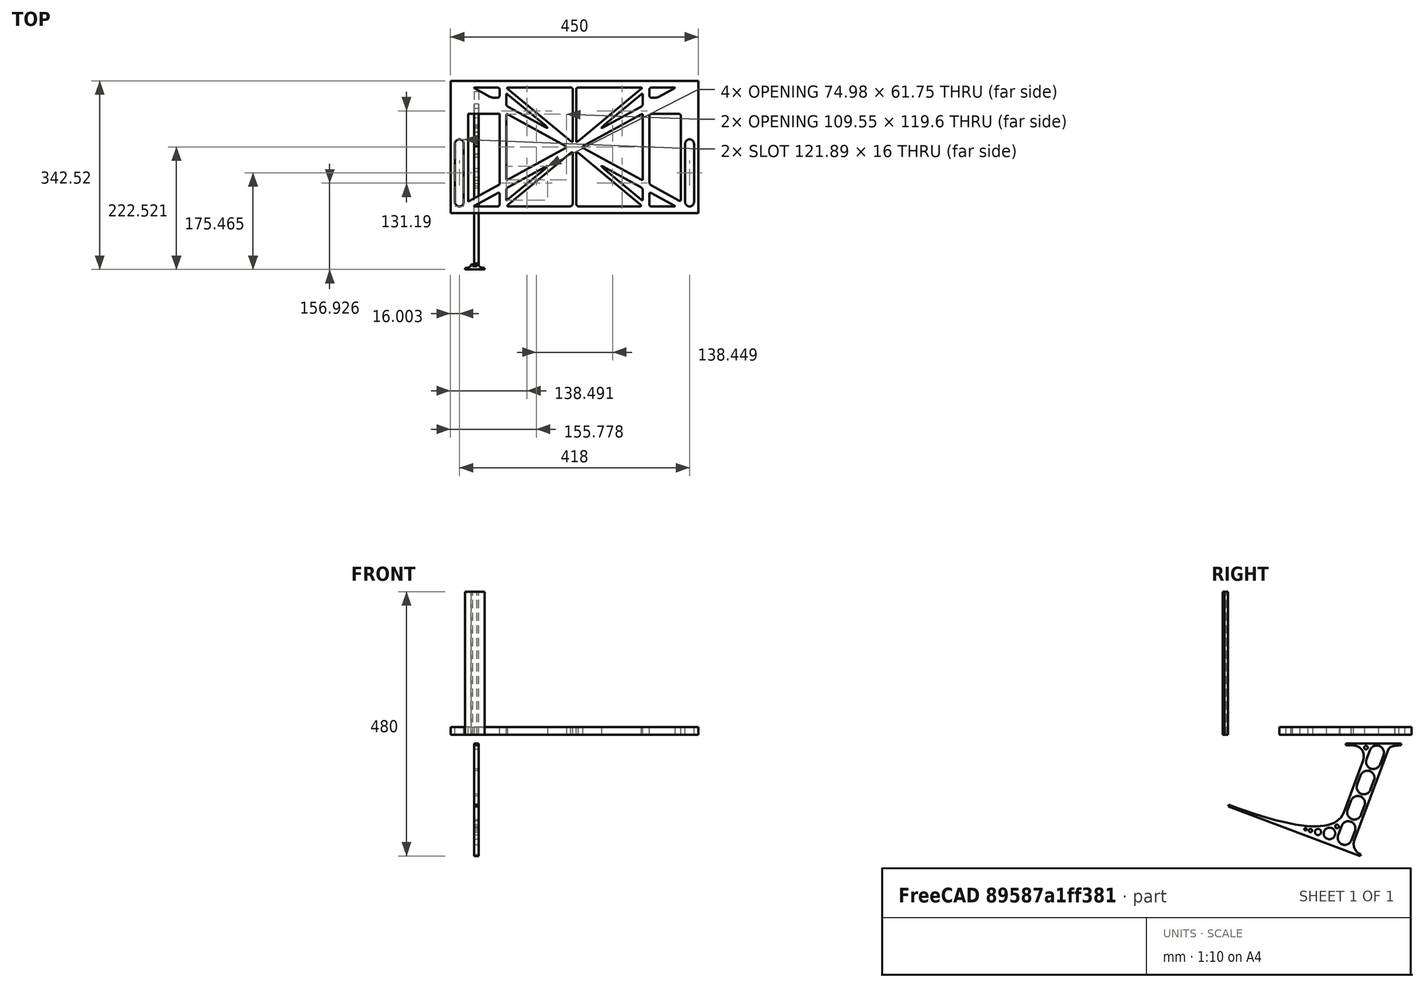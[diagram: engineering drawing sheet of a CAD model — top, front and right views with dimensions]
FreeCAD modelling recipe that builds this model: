
FCSTD DOCUMENT  (FreeCAD 0.19R0.19.2)
Label: laptopStand142FCStd
License: All rights reserved
LicenseURL: http://en.wikipedia.org/wiki/All_rights_reserved
objects: Sketcher::SketchObject×4, Part::Extrusion×3
note: 7 computed .brp shape members not serialized (recipe doc carries the construction recipe); baked Part::Feature solids carry a one-line shape summary decoded from their .brp

FEATURE [Sketcher::SketchObject] Sketch
  FullyConstrained = false
  sketch-geometry (349):
    g0: LineSegment StartX=-10.9272 StartY=-82.7794 StartZ=0 EndX=46.0728 EndY=-51.4823 EndZ=0
    g1: LineSegment StartX=-10.9272 StartY=76.4095 StartZ=0 EndX=-10.9272 EndY=-82.7794 EndZ=0
    g2: LineSegment StartX=46.0728 StartY=76.4095 StartZ=0 EndX=46.0728 EndY=-51.4823 EndZ=0
    g3: LineSegment StartX=-42.9272 StartY=136.221 StartZ=0 EndX=-42.9272 EndY=-103.779 EndZ=0
    g4: LineSegment StartX=407.073 StartY=136.221 StartZ=0 EndX=407.073 EndY=-103.779 EndZ=0
    g5: ArcOfCircle CenterX=-26.9272 CenterY=-83.7794 CenterZ=0 NormalX=0 NormalY=0 NormalZ=1 AngleXU=0 Radius=8 StartAngle=3.14159 EndAngle=6.28319
    g6: ArcOfCircle CenterX=391.073 CenterY=22.1087 CenterZ=0 NormalX=0 NormalY=0 NormalZ=1 AngleXU=0 Radius=8 StartAngle=-4.4e-15 EndAngle=3.14159
    g7: LineSegment StartX=399.073 StartY=22.1087 StartZ=0 EndX=399.073 EndY=-83.7794 EndZ=0
    g8: LineSegment StartX=383.073 StartY=22.1087 StartZ=0 EndX=383.073 EndY=-83.7794 EndZ=0
    g9: ArcOfCircle CenterX=391.073 CenterY=-83.7794 CenterZ=0 NormalX=0 NormalY=0 NormalZ=1 AngleXU=0 Radius=8 StartAngle=3.14159 EndAngle=6.28319
    g10: Circle CenterX=175.022 CenterY=27.0628 CenterZ=0 NormalX=0 NormalY=0 NormalZ=1 AngleXU=0 Radius=1
    g11: Circle CenterX=179.022 CenterY=24.8665 CenterZ=0 NormalX=0 NormalY=0 NormalZ=1 AngleXU=0 Radius=1
    g12: Circle CenterX=179.022 CenterY=27.0628 CenterZ=0 NormalX=0 NormalY=0 NormalZ=1 AngleXU=0 Radius=1
    g13: BSplineCurve PolesCount=3 KnotsCount=2 Degree=2 IsPeriodic=0
    g14: GeomPoint X=175.022 Y=27.0628 Z=0
    g15: GeomPoint X=179.022 Y=27.0628 Z=0
    g16: Circle CenterX=189.124 CenterY=27.0628 CenterZ=0 NormalX=0 NormalY=0 NormalZ=1 AngleXU=0 Radius=1
    g17: Circle CenterX=185.124 CenterY=24.8665 CenterZ=0 NormalX=0 NormalY=0 NormalZ=1 AngleXU=0 Radius=1
    g18: Circle CenterX=185.124 CenterY=27.0628 CenterZ=0 NormalX=0 NormalY=0 NormalZ=1 AngleXU=0 Radius=1
    g19: BSplineCurve PolesCount=3 KnotsCount=2 Degree=2 IsPeriodic=0
    g20: GeomPoint X=189.124 Y=27.0628 Z=0
    g21: GeomPoint X=185.124 Y=27.0628 Z=0
    g22: Circle CenterX=175.022 CenterY=5.37834 CenterZ=0 NormalX=0 NormalY=0 NormalZ=1 AngleXU=0 Radius=1
    g23: Circle CenterX=179.022 CenterY=7.57463 CenterZ=0 NormalX=0 NormalY=0 NormalZ=1 AngleXU=0 Radius=1
    g24: Circle CenterX=179.022 CenterY=5.34704 CenterZ=0 NormalX=0 NormalY=0 NormalZ=1 AngleXU=0 Radius=1
    g25: BSplineCurve PolesCount=3 KnotsCount=2 Degree=2 IsPeriodic=0
    g26: GeomPoint X=175.022 Y=5.37834 Z=0
    g27: GeomPoint X=179.022 Y=5.34704 Z=0
    g28: Circle CenterX=189.124 CenterY=5.37834 CenterZ=0 NormalX=0 NormalY=0 NormalZ=1 AngleXU=0 Radius=1
    g29: Circle CenterX=185.124 CenterY=7.57463 CenterZ=0 NormalX=0 NormalY=0 NormalZ=1 AngleXU=0 Radius=1
    g30: Circle CenterX=185.124 CenterY=5.34704 CenterZ=0 NormalX=0 NormalY=0 NormalZ=1 AngleXU=0 Radius=1
    g31: BSplineCurve PolesCount=3 KnotsCount=2 Degree=2 IsPeriodic=0
    g32: GeomPoint X=189.124 Y=5.37834 Z=0
    g33: GeomPoint X=185.124 Y=5.34704 Z=0
    g34: Circle CenterX=165.871 CenterY=18.1458 CenterZ=0 NormalX=0 NormalY=0 NormalZ=1 AngleXU=0 Radius=1
    g35: Circle CenterX=169.377 CenterY=16.2206 CenterZ=0 NormalX=0 NormalY=0 NormalZ=1 AngleXU=0 Radius=1
    g36: Circle CenterX=165.871 CenterY=14.2954 CenterZ=0 NormalX=0 NormalY=0 NormalZ=1 AngleXU=0 Radius=1
    g37: BSplineCurve PolesCount=3 KnotsCount=2 Degree=2 IsPeriodic=0
    g38: GeomPoint X=165.871 Y=18.1458 Z=0
    g39: GeomPoint X=165.871 Y=14.2954 Z=0
    g40: Circle CenterX=198.275 CenterY=18.1458 CenterZ=0 NormalX=0 NormalY=0 NormalZ=1 AngleXU=0 Radius=1
    g41: Circle CenterX=194.768 CenterY=16.2206 CenterZ=0 NormalX=0 NormalY=0 NormalZ=1 AngleXU=0 Radius=1
    g42: Circle CenterX=198.275 CenterY=14.2954 CenterZ=0 NormalX=0 NormalY=0 NormalZ=1 AngleXU=0 Radius=1
    g43: BSplineCurve PolesCount=3 KnotsCount=2 Degree=2 IsPeriodic=0
    g44: GeomPoint X=198.275 Y=18.1458 Z=0
    g45: GeomPoint X=198.275 Y=14.2954 Z=0
    g46: LineSegment StartX=407.073 StartY=-103.779 StartZ=0 EndX=-42.9272 EndY=-103.779 EndZ=0
    g47: LineSegment StartX=407.073 StartY=136.221 StartZ=0 EndX=-42.9272 EndY=136.221 EndZ=0
    g48: LineSegment StartX=46.0728 StartY=76.4095 StartZ=0 EndX=-10.9272 EndY=76.4095 EndZ=0
    g49: Circle CenterX=125.607 CenterY=54.1951 CenterZ=0 NormalX=0 NormalY=0 NormalZ=1 AngleXU=0 Radius=1
    g50: Circle CenterX=139.632 CenterY=46.4944 CenterZ=0 NormalX=0 NormalY=0 NormalZ=1 AngleXU=0 Radius=1
    g51: Circle CenterX=127.326 CenterY=56.7187 CenterZ=0 NormalX=0 NormalY=0 NormalZ=1 AngleXU=0 Radius=1
    g52: BSplineCurve PolesCount=3 KnotsCount=2 Degree=2 IsPeriodic=0
    g53: GeomPoint X=125.607 Y=54.1951 Z=0
    g54: GeomPoint X=127.326 Y=56.7187 Z=0
    g55: Circle CenterX=236.821 CenterY=56.7187 CenterZ=0 NormalX=0 NormalY=0 NormalZ=1 AngleXU=0 Radius=1
    g56: Circle CenterX=224.513 CenterY=46.4944 CenterZ=0 NormalX=0 NormalY=0 NormalZ=1 AngleXU=0 Radius=1
    g57: Circle CenterX=238.538 CenterY=54.1951 CenterZ=0 NormalX=0 NormalY=0 NormalZ=1 AngleXU=0 Radius=1
    g58: BSplineCurve PolesCount=3 KnotsCount=2 Degree=2 IsPeriodic=0
    g59: GeomPoint X=236.821 Y=56.7187 Z=0
    g60: GeomPoint X=238.538 Y=54.1951 Z=0
    g61: Circle CenterX=238.538 CenterY=-21.7539 CenterZ=0 NormalX=0 NormalY=0 NormalZ=1 AngleXU=0 Radius=1
    g62: Circle CenterX=224.513 CenterY=-14.0532 CenterZ=0 NormalX=0 NormalY=0 NormalZ=1 AngleXU=0 Radius=1
    g63: Circle CenterX=236.821 CenterY=-24.2775 CenterZ=0 NormalX=0 NormalY=0 NormalZ=1 AngleXU=0 Radius=1
    g64: BSplineCurve PolesCount=3 KnotsCount=2 Degree=2 IsPeriodic=0
    g65: GeomPoint X=238.538 Y=-21.7539 Z=0
    g66: GeomPoint X=236.821 Y=-24.2775 Z=0
    g67: Circle CenterX=125.607 CenterY=-21.7539 CenterZ=0 NormalX=0 NormalY=0 NormalZ=1 AngleXU=0 Radius=1
    g68: Circle CenterX=139.632 CenterY=-14.0532 CenterZ=0 NormalX=0 NormalY=0 NormalZ=1 AngleXU=0 Radius=1
    g69: Circle CenterX=127.325 CenterY=-24.2775 CenterZ=0 NormalX=0 NormalY=0 NormalZ=1 AngleXU=0 Radius=1
    g70: BSplineCurve PolesCount=3 KnotsCount=2 Degree=2 IsPeriodic=0
    g71: GeomPoint X=125.607 Y=-21.7539 Z=0
    g72: GeomPoint X=127.325 Y=-24.2775 Z=0
    g73: Circle CenterX=302.996 CenterY=111.695 CenterZ=0 NormalX=0 NormalY=0 NormalZ=1 AngleXU=0 Radius=1
    g74: Circle CenterX=306.073 CenterY=114.251 CenterZ=0 NormalX=0 NormalY=0 NormalZ=1 AngleXU=0 Radius=1
    g75: Circle CenterX=306.073 CenterY=110.251 CenterZ=0 NormalX=0 NormalY=0 NormalZ=1 AngleXU=0 Radius=1
    g76: BSplineCurve PolesCount=3 KnotsCount=2 Degree=2 IsPeriodic=0
    g77: GeomPoint X=302.996 Y=111.695 Z=0
    g78: GeomPoint X=306.073 Y=110.251 Z=0
    g79: Circle CenterX=306.073 CenterY=95.2763 CenterZ=0 NormalX=0 NormalY=0 NormalZ=1 AngleXU=0 Radius=1
    g80: Circle CenterX=306.073 CenterY=91.2763 CenterZ=0 NormalX=0 NormalY=0 NormalZ=1 AngleXU=0 Radius=1
    g81: Circle CenterX=302.567 CenterY=89.3511 CenterZ=0 NormalX=0 NormalY=0 NormalZ=1 AngleXU=0 Radius=1
    g82: BSplineCurve PolesCount=3 KnotsCount=2 Degree=2 IsPeriodic=0
    g83: GeomPoint X=306.073 Y=95.2763 Z=0
    g84: GeomPoint X=302.567 Y=89.3511 Z=0
    g85: LineSegment StartX=306.073 StartY=110.251 StartZ=0 EndX=306.073 EndY=95.2763 EndZ=0
    g86: LineSegment StartX=302.996 StartY=111.695 StartZ=0 EndX=236.821 EndY=56.7187 EndZ=0
    g87: LineSegment StartX=238.538 StartY=54.1951 StartZ=0 EndX=302.567 EndY=89.3511 EndZ=0
    g88: Circle CenterX=61.1496 CenterY=111.695 CenterZ=0 NormalX=0 NormalY=0 NormalZ=1 AngleXU=0 Radius=1
    g89: Circle CenterX=58.0728 CenterY=114.251 CenterZ=0 NormalX=0 NormalY=0 NormalZ=1 AngleXU=0 Radius=1
    g90: Circle CenterX=58.0728 CenterY=110.251 CenterZ=0 NormalX=0 NormalY=0 NormalZ=1 AngleXU=0 Radius=1
    g91: BSplineCurve PolesCount=3 KnotsCount=2 Degree=2 IsPeriodic=0
    g92: GeomPoint X=61.1496 Y=111.695 Z=0
    g93: GeomPoint X=58.0728 Y=110.251 Z=0
    g94: Circle CenterX=61.5791 CenterY=89.3511 CenterZ=0 NormalX=0 NormalY=0 NormalZ=1 AngleXU=0 Radius=1
    g95: Circle CenterX=58.0728 CenterY=91.2763 CenterZ=0 NormalX=0 NormalY=0 NormalZ=1 AngleXU=0 Radius=1
    g96: Circle CenterX=58.0728 CenterY=95.2763 CenterZ=0 NormalX=0 NormalY=0 NormalZ=1 AngleXU=0 Radius=1
    g97: BSplineCurve PolesCount=3 KnotsCount=2 Degree=2 IsPeriodic=0
    g98: GeomPoint X=61.5791 Y=89.3511 Z=0
    g99: GeomPoint X=58.0728 Y=95.2763 Z=0
    g100: LineSegment StartX=58.0728 StartY=110.251 StartZ=0 EndX=58.0728 EndY=95.2763 EndZ=0
    g101: LineSegment StartX=61.1496 StartY=111.695 StartZ=0 EndX=127.326 EndY=56.7187 EndZ=0
    g102: LineSegment StartX=125.607 StartY=54.1951 StartZ=0 EndX=61.5791 EndY=89.3511 EndZ=0
    g103: Circle CenterX=61.5791 CenterY=-56.9099 CenterZ=0 NormalX=0 NormalY=0 NormalZ=1 AngleXU=0 Radius=1
    g104: Circle CenterX=58.0728 CenterY=-58.8351 CenterZ=0 NormalX=0 NormalY=0 NormalZ=1 AngleXU=0 Radius=1
    g105: Circle CenterX=58.0728 CenterY=-62.8351 CenterZ=0 NormalX=0 NormalY=0 NormalZ=1 AngleXU=0 Radius=1
    g106: BSplineCurve PolesCount=3 KnotsCount=2 Degree=2 IsPeriodic=0
    g107: GeomPoint X=61.5791 Y=-56.9099 Z=0
    g108: GeomPoint X=58.0728 Y=-62.8351 Z=0
    g109: Circle CenterX=58.0728 CenterY=-77.8102 CenterZ=0 NormalX=0 NormalY=0 NormalZ=1 AngleXU=0 Radius=1
    g110: Circle CenterX=58.0728 CenterY=-81.8102 CenterZ=0 NormalX=0 NormalY=0 NormalZ=1 AngleXU=0 Radius=1
    g111: Circle CenterX=61.1496 CenterY=-79.2541 CenterZ=0 NormalX=0 NormalY=0 NormalZ=1 AngleXU=0 Radius=1
    g112: BSplineCurve PolesCount=3 KnotsCount=2 Degree=2 IsPeriodic=0
    g113: GeomPoint X=58.0728 Y=-77.8102 Z=0
    g114: GeomPoint X=61.1496 Y=-79.2541 Z=0
    g115: LineSegment StartX=58.0728 StartY=-62.8351 StartZ=0 EndX=58.0728 EndY=-77.8102 EndZ=0
    g116: LineSegment StartX=61.1496 StartY=-79.2541 StartZ=0 EndX=127.325 EndY=-24.2775 EndZ=0
    g117: LineSegment StartX=125.607 StartY=-21.7539 StartZ=0 EndX=61.5791 EndY=-56.9099 EndZ=0
    g118: Circle CenterX=302.567 CenterY=-56.9099 CenterZ=0 NormalX=0 NormalY=0 NormalZ=1 AngleXU=0 Radius=1
    g119: Circle CenterX=306.073 CenterY=-58.8351 CenterZ=0 NormalX=0 NormalY=0 NormalZ=1 AngleXU=0 Radius=1
    g120: Circle CenterX=306.073 CenterY=-62.8351 CenterZ=0 NormalX=0 NormalY=0 NormalZ=1 AngleXU=0 Radius=1
    g121: BSplineCurve PolesCount=3 KnotsCount=2 Degree=2 IsPeriodic=0
    g122: GeomPoint X=302.567 Y=-56.9099 Z=0
    g123: GeomPoint X=306.073 Y=-62.8351 Z=0
    g124: Circle CenterX=302.996 CenterY=-79.2541 CenterZ=0 NormalX=0 NormalY=0 NormalZ=1 AngleXU=0 Radius=1
    g125: Circle CenterX=306.073 CenterY=-81.8102 CenterZ=0 NormalX=0 NormalY=0 NormalZ=1 AngleXU=0 Radius=1
    g126: Circle CenterX=306.073 CenterY=-77.8102 CenterZ=0 NormalX=0 NormalY=0 NormalZ=1 AngleXU=0 Radius=1
    g127: BSplineCurve PolesCount=3 KnotsCount=2 Degree=2 IsPeriodic=0
    g128: GeomPoint X=302.996 Y=-79.2541 Z=0
    g129: GeomPoint X=306.073 Y=-77.8102 Z=0
    g130: LineSegment StartX=306.073 StartY=-62.8351 StartZ=0 EndX=306.073 EndY=-77.8102 EndZ=0
    g131: LineSegment StartX=302.996 StartY=-79.2541 StartZ=0 EndX=236.821 EndY=-24.2775 EndZ=0
    g132: LineSegment StartX=238.538 StartY=-21.7539 StartZ=0 EndX=302.567 EndY=-56.9099 EndZ=0
    g133: Circle CenterX=61.6457 CenterY=-88.8112 CenterZ=0 NormalX=0 NormalY=0 NormalZ=1 AngleXU=0 Radius=1
    g134: Circle CenterX=58.0728 CenterY=-91.7794 CenterZ=0 NormalX=0 NormalY=0 NormalZ=1 AngleXU=0 Radius=1
    g135: Circle CenterX=63.9135 CenterY=-91.7794 CenterZ=0 NormalX=0 NormalY=0 NormalZ=1 AngleXU=0 Radius=1
    g136: BSplineCurve PolesCount=3 KnotsCount=2 Degree=2 IsPeriodic=0
    g137: GeomPoint X=61.6457 Y=-88.8112 Z=0
    g138: GeomPoint X=63.9135 Y=-91.7794 Z=0
    g139: Circle CenterX=179.022 CenterY=-85.8163 CenterZ=0 NormalX=0 NormalY=0 NormalZ=1 AngleXU=0 Radius=1
    g140: Circle CenterX=179.022 CenterY=-91.7794 CenterZ=0 NormalX=0 NormalY=0 NormalZ=1 AngleXU=0 Radius=1
    g141: Circle CenterX=171.895 CenterY=-91.7794 CenterZ=0 NormalX=0 NormalY=0 NormalZ=1 AngleXU=0 Radius=1
    g142: BSplineCurve PolesCount=3 KnotsCount=2 Degree=2 IsPeriodic=0
    g143: GeomPoint X=179.022 Y=-85.8163 Z=0
    g144: GeomPoint X=171.895 Y=-91.7794 Z=0
    g145: Circle CenterX=185.124 CenterY=-86.2028 CenterZ=0 NormalX=0 NormalY=0 NormalZ=1 AngleXU=0 Radius=1
    g146: Circle CenterX=185.124 CenterY=-91.7794 CenterZ=0 NormalX=0 NormalY=0 NormalZ=1 AngleXU=0 Radius=1
    g147: Circle CenterX=191.747 CenterY=-91.7794 CenterZ=0 NormalX=0 NormalY=0 NormalZ=1 AngleXU=0 Radius=1
    g148: BSplineCurve PolesCount=3 KnotsCount=2 Degree=2 IsPeriodic=0
    g149: GeomPoint X=185.124 Y=-86.2028 Z=0
    g150: GeomPoint X=191.747 Y=-91.7794 Z=0
    g151: Circle CenterX=299.888 CenterY=-86.6413 CenterZ=0 NormalX=0 NormalY=0 NormalZ=1 AngleXU=0 Radius=1
    g152: Circle CenterX=306.073 CenterY=-91.7794 CenterZ=0 NormalX=0 NormalY=0 NormalZ=1 AngleXU=0 Radius=1
    g153: Circle CenterX=298.776 CenterY=-91.7794 CenterZ=0 NormalX=0 NormalY=0 NormalZ=1 AngleXU=0 Radius=1
    g154: BSplineCurve PolesCount=3 KnotsCount=2 Degree=2 IsPeriodic=0
    g155: GeomPoint X=299.888 Y=-86.6413 Z=0
    g156: GeomPoint X=298.776 Y=-91.7794 Z=0
    g157: LineSegment StartX=189.124 StartY=5.37834 StartZ=0 EndX=299.888 EndY=-86.6413 EndZ=0
    g158: LineSegment StartX=298.776 StartY=-91.7794 StartZ=0 EndX=191.747 EndY=-91.7794 EndZ=0
    g159: LineSegment StartX=185.124 StartY=-86.2028 StartZ=0 EndX=185.124 EndY=5.34704 EndZ=0
    g160: LineSegment StartX=179.022 StartY=5.34704 StartZ=0 EndX=179.022 EndY=-85.8163 EndZ=0
    g161: LineSegment StartX=171.895 StartY=-91.7794 StartZ=0 EndX=63.9135 EndY=-91.7794 EndZ=0
    g162: LineSegment StartX=61.6457 StartY=-88.8112 StartZ=0 EndX=175.022 EndY=5.37834 EndZ=0
    g163: Circle CenterX=302.073 CenterY=124.221 CenterZ=0 NormalX=0 NormalY=0 NormalZ=1 AngleXU=0 Radius=1
    g164: Circle CenterX=306.073 CenterY=124.221 CenterZ=0 NormalX=0 NormalY=0 NormalZ=1 AngleXU=0 Radius=1
    g165: Circle CenterX=302.996 CenterY=121.665 CenterZ=0 NormalX=0 NormalY=0 NormalZ=1 AngleXU=0 Radius=1
    g166: BSplineCurve PolesCount=3 KnotsCount=2 Degree=2 IsPeriodic=0
    g167: GeomPoint X=302.073 Y=124.221 Z=0
    g168: GeomPoint X=302.996 Y=121.665 Z=0
    g169: Circle CenterX=189.124 CenterY=124.221 CenterZ=0 NormalX=0 NormalY=0 NormalZ=1 AngleXU=0 Radius=1
    g170: Circle CenterX=185.124 CenterY=124.221 CenterZ=0 NormalX=0 NormalY=0 NormalZ=1 AngleXU=0 Radius=1
    g171: Circle CenterX=185.124 CenterY=120.221 CenterZ=0 NormalX=0 NormalY=0 NormalZ=1 AngleXU=0 Radius=1
    g172: BSplineCurve PolesCount=3 KnotsCount=2 Degree=2 IsPeriodic=0
    g173: GeomPoint X=189.124 Y=124.221 Z=0
    g174: GeomPoint X=185.124 Y=120.221 Z=0
    g175: Circle CenterX=175.022 CenterY=124.221 CenterZ=0 NormalX=0 NormalY=0 NormalZ=1 AngleXU=0 Radius=1
    g176: Circle CenterX=179.022 CenterY=124.221 CenterZ=0 NormalX=0 NormalY=0 NormalZ=1 AngleXU=0 Radius=1
    g177: Circle CenterX=179.022 CenterY=120.221 CenterZ=0 NormalX=0 NormalY=0 NormalZ=1 AngleXU=0 Radius=1
    g178: BSplineCurve PolesCount=3 KnotsCount=2 Degree=2 IsPeriodic=0
    g179: GeomPoint X=175.022 Y=124.221 Z=0
    g180: GeomPoint X=179.022 Y=120.221 Z=0
    g181: Circle CenterX=62.0728 CenterY=124.221 CenterZ=0 NormalX=0 NormalY=0 NormalZ=1 AngleXU=0 Radius=1
    g182: Circle CenterX=58.0728 CenterY=124.221 CenterZ=0 NormalX=0 NormalY=0 NormalZ=1 AngleXU=0 Radius=1
    g183: Circle CenterX=61.1496 CenterY=121.665 CenterZ=0 NormalX=0 NormalY=0 NormalZ=1 AngleXU=0 Radius=1
    g184: BSplineCurve PolesCount=3 KnotsCount=2 Degree=2 IsPeriodic=0
    g185: GeomPoint X=62.0728 Y=124.221 Z=0
    g186: GeomPoint X=61.1496 Y=121.665 Z=0
    g187: LineSegment StartX=62.0728 StartY=124.221 StartZ=0 EndX=175.022 EndY=124.221 EndZ=0
    g188: LineSegment StartX=179.022 StartY=120.221 StartZ=0 EndX=179.022 EndY=27.0628 EndZ=0
    g189: LineSegment StartX=185.124 StartY=27.0628 StartZ=0 EndX=185.124 EndY=120.221 EndZ=0
    g190: LineSegment StartX=189.124 StartY=124.221 StartZ=0 EndX=302.073 EndY=124.221 EndZ=0
    g191: LineSegment StartX=302.996 StartY=121.665 StartZ=0 EndX=189.124 EndY=27.0628 EndZ=0
    g192: LineSegment StartX=175.022 StartY=27.0628 StartZ=0 EndX=61.1496 EndY=121.665 EndZ=0
    g193: Circle CenterX=61.5791 CenterY=75.4095 CenterZ=0 NormalX=0 NormalY=0 NormalZ=1 AngleXU=0 Radius=1
    g194: Circle CenterX=58.0728 CenterY=77.3346 CenterZ=0 NormalX=0 NormalY=0 NormalZ=1 AngleXU=0 Radius=1
    g195: Circle CenterX=58.0728 CenterY=73.3346 CenterZ=0 NormalX=0 NormalY=0 NormalZ=1 AngleXU=0 Radius=1
    g196: BSplineCurve PolesCount=3 KnotsCount=2 Degree=2 IsPeriodic=0
    g197: GeomPoint X=61.5791 Y=75.4095 Z=0
    g198: GeomPoint X=58.0728 Y=73.3346 Z=0
    g199: Circle CenterX=58.0728 CenterY=-40.8935 CenterZ=0 NormalX=0 NormalY=0 NormalZ=1 AngleXU=0 Radius=1
    g200: Circle CenterX=58.0728 CenterY=-44.8935 CenterZ=0 NormalX=0 NormalY=0 NormalZ=1 AngleXU=0 Radius=1
    g201: Circle CenterX=61.5791 CenterY=-42.9683 CenterZ=0 NormalX=0 NormalY=0 NormalZ=1 AngleXU=0 Radius=1
    g202: BSplineCurve PolesCount=3 KnotsCount=2 Degree=2 IsPeriodic=0
    g203: GeomPoint X=58.0728 Y=-40.8935 Z=0
    g204: GeomPoint X=61.5791 Y=-42.9683 Z=0
    g205: LineSegment StartX=61.5791 StartY=-42.9683 StartZ=0 EndX=165.871 EndY=14.2954 EndZ=0
    g206: LineSegment StartX=165.871 StartY=18.1458 StartZ=0 EndX=61.5791 EndY=75.4095 EndZ=0
    g207: LineSegment StartX=58.0728 StartY=73.3346 StartZ=0 EndX=58.0728 EndY=-40.8935 EndZ=0
    g208: Circle CenterX=302.567 CenterY=-42.9683 CenterZ=0 NormalX=0 NormalY=0 NormalZ=1 AngleXU=0 Radius=1
    g209: Circle CenterX=306.073 CenterY=-44.8935 CenterZ=0 NormalX=0 NormalY=0 NormalZ=1 AngleXU=0 Radius=1
    g210: Circle CenterX=306.073 CenterY=-40.8935 CenterZ=0 NormalX=0 NormalY=0 NormalZ=1 AngleXU=0 Radius=1
    g211: BSplineCurve PolesCount=3 KnotsCount=2 Degree=2 IsPeriodic=0
    g212: GeomPoint X=302.567 Y=-42.9683 Z=0
    g213: GeomPoint X=306.073 Y=-40.8935 Z=0
    g214: Circle CenterX=306.073 CenterY=73.3346 CenterZ=0 NormalX=0 NormalY=0 NormalZ=1 AngleXU=0 Radius=1
    g215: Circle CenterX=306.073 CenterY=77.3346 CenterZ=0 NormalX=0 NormalY=0 NormalZ=1 AngleXU=0 Radius=1
    g216: Circle CenterX=302.567 CenterY=75.4095 CenterZ=0 NormalX=0 NormalY=0 NormalZ=1 AngleXU=0 Radius=1
    g217: BSplineCurve PolesCount=3 KnotsCount=2 Degree=2 IsPeriodic=0
    g218: GeomPoint X=306.073 Y=73.3346 Z=0
    g219: GeomPoint X=302.567 Y=75.4095 Z=0
    g220: LineSegment StartX=302.567 StartY=-42.9683 StartZ=0 EndX=198.275 EndY=14.2954 EndZ=0
    g221: LineSegment StartX=198.275 StartY=18.1458 StartZ=0 EndX=302.567 EndY=75.4095 EndZ=0
    g222: LineSegment StartX=306.073 StartY=73.3346 StartZ=0 EndX=306.073 EndY=-40.8935 EndZ=0
    g223: LineSegment StartX=322.073 StartY=105.865 StartZ=0 EndX=328.643 EndY=105.865 EndZ=0
    g224: LineSegment StartX=318.073 StartY=120.221 StartZ=0 EndX=318.073 EndY=109.865 EndZ=0
    g225: LineSegment StartX=336.157 StartY=107.779 StartZ=0 EndX=362.567 EndY=122.294 EndZ=0
    g226: Circle CenterX=362.073 CenterY=124.221 CenterZ=0 NormalX=0 NormalY=0 NormalZ=1 AngleXU=0 Radius=1
    g227: Circle CenterX=366.073 CenterY=124.221 CenterZ=0 NormalX=0 NormalY=0 NormalZ=1 AngleXU=0 Radius=1
    g228: Circle CenterX=362.567 CenterY=122.294 CenterZ=0 NormalX=0 NormalY=0 NormalZ=1 AngleXU=0 Radius=1
    g229: BSplineCurve PolesCount=3 KnotsCount=2 Degree=2 IsPeriodic=0
    g230: GeomPoint X=362.073 Y=124.221 Z=0
    g231: GeomPoint X=362.567 Y=122.294 Z=0
    g232: Circle CenterX=322.073 CenterY=124.221 CenterZ=0 NormalX=0 NormalY=0 NormalZ=1 AngleXU=0 Radius=1
    g233: Circle CenterX=318.073 CenterY=124.221 CenterZ=0 NormalX=0 NormalY=0 NormalZ=1 AngleXU=0 Radius=1
    g234: Circle CenterX=318.073 CenterY=120.221 CenterZ=0 NormalX=0 NormalY=0 NormalZ=1 AngleXU=0 Radius=1
    g235: BSplineCurve PolesCount=3 KnotsCount=2 Degree=2 IsPeriodic=0
    g236: GeomPoint X=322.073 Y=124.221 Z=0
    g237: GeomPoint X=318.073 Y=120.221 Z=0
    g238: Circle CenterX=322.073 CenterY=105.865 CenterZ=0 NormalX=0 NormalY=0 NormalZ=1 AngleXU=0 Radius=1
    g239: Circle CenterX=318.073 CenterY=105.865 CenterZ=0 NormalX=0 NormalY=0 NormalZ=1 AngleXU=0 Radius=1
    g240: Circle CenterX=318.073 CenterY=109.865 CenterZ=0 NormalX=0 NormalY=0 NormalZ=1 AngleXU=0 Radius=1
    g241: BSplineCurve PolesCount=3 KnotsCount=2 Degree=2 IsPeriodic=0
    g242: GeomPoint X=322.073 Y=105.865 Z=0
    g243: GeomPoint X=318.073 Y=109.865 Z=0
    g244: Circle CenterX=336.157 CenterY=107.779 CenterZ=0 NormalX=0 NormalY=0 NormalZ=1 AngleXU=0 Radius=1
    g245: Circle CenterX=332.651 CenterY=105.853 CenterZ=0 NormalX=0 NormalY=0 NormalZ=1 AngleXU=0 Radius=1
    g246: Circle CenterX=328.643 CenterY=105.865 CenterZ=0 NormalX=0 NormalY=0 NormalZ=1 AngleXU=0 Radius=1
    g247: BSplineCurve PolesCount=3 KnotsCount=2 Degree=2 IsPeriodic=0
    g248: GeomPoint X=336.157 Y=107.779 Z=0
    g249: GeomPoint X=328.643 Y=105.865 Z=0
    g250: LineSegment StartX=322.073 StartY=124.221 StartZ=0 EndX=362.073 EndY=124.221 EndZ=0
    g251: Circle CenterX=371.567 CenterY=-80.8644 CenterZ=0 NormalX=0 NormalY=0 NormalZ=1 AngleXU=0 Radius=1
    g252: Circle CenterX=375.073 CenterY=-82.7896 CenterZ=0 NormalX=0 NormalY=0 NormalZ=1 AngleXU=0 Radius=1
    g253: Circle CenterX=375.073 CenterY=-78.7896 CenterZ=0 NormalX=0 NormalY=0 NormalZ=1 AngleXU=0 Radius=1
    g254: BSplineCurve PolesCount=3 KnotsCount=2 Degree=2 IsPeriodic=0
    g255: GeomPoint X=371.567 Y=-80.8644 Z=0
    g256: GeomPoint X=375.073 Y=-78.7896 Z=0
    g257: Circle CenterX=321.579 CenterY=-53.4075 CenterZ=0 NormalX=0 NormalY=0 NormalZ=1 AngleXU=0 Radius=1
    g258: Circle CenterX=318.073 CenterY=-51.4823 CenterZ=0 NormalX=0 NormalY=0 NormalZ=1 AngleXU=0 Radius=1
    g259: Circle CenterX=318.073 CenterY=-47.4805 CenterZ=0 NormalX=0 NormalY=0 NormalZ=1 AngleXU=0 Radius=1
    g260: BSplineCurve PolesCount=3 KnotsCount=2 Degree=2 IsPeriodic=0
    g261: GeomPoint X=321.579 Y=-53.4075 Z=0
    g262: GeomPoint X=318.073 Y=-47.4805 Z=0
    g263: LineSegment StartX=371.567 StartY=-80.8644 StartZ=0 EndX=321.579 EndY=-53.4075 EndZ=0
    g264: Circle CenterX=321.579 CenterY=-67.3492 CenterZ=0 NormalX=0 NormalY=0 NormalZ=1 AngleXU=0 Radius=1
    g265: Circle CenterX=318.073 CenterY=-65.424 CenterZ=0 NormalX=0 NormalY=0 NormalZ=1 AngleXU=0 Radius=1
    g266: Circle CenterX=318.073 CenterY=-69.424 CenterZ=0 NormalX=0 NormalY=0 NormalZ=1 AngleXU=0 Radius=1
    g267: BSplineCurve PolesCount=3 KnotsCount=2 Degree=2 IsPeriodic=0
    g268: GeomPoint X=321.579 Y=-67.3492 Z=0
    g269: GeomPoint X=318.073 Y=-69.424 Z=0
    g270: Circle CenterX=362.567 CenterY=-89.8542 CenterZ=0 NormalX=0 NormalY=0 NormalZ=1 AngleXU=0 Radius=1
    g271: Circle CenterX=366.073 CenterY=-91.7794 CenterZ=0 NormalX=0 NormalY=0 NormalZ=1 AngleXU=0 Radius=1
    g272: Circle CenterX=362.073 CenterY=-91.7794 CenterZ=0 NormalX=0 NormalY=0 NormalZ=1 AngleXU=0 Radius=1
    g273: BSplineCurve PolesCount=3 KnotsCount=2 Degree=2 IsPeriodic=0
    g274: GeomPoint X=362.567 Y=-89.8542 Z=0
    g275: GeomPoint X=362.073 Y=-91.7794 Z=0
    g276: Circle CenterX=322.073 CenterY=-91.7794 CenterZ=0 NormalX=0 NormalY=0 NormalZ=1 AngleXU=0 Radius=1
    g277: Circle CenterX=318.073 CenterY=-91.7794 CenterZ=0 NormalX=0 NormalY=0 NormalZ=1 AngleXU=0 Radius=1
    g278: Circle CenterX=318.073 CenterY=-87.7794 CenterZ=0 NormalX=0 NormalY=0 NormalZ=1 AngleXU=0 Radius=1
    g279: BSplineCurve PolesCount=3 KnotsCount=2 Degree=2 IsPeriodic=0
    g280: GeomPoint X=322.073 Y=-91.7794 Z=0
    g281: GeomPoint X=318.073 Y=-87.7794 Z=0
    g282: LineSegment StartX=362.567 StartY=-89.8542 StartZ=0 EndX=321.579 EndY=-67.3492 EndZ=0
    g283: LineSegment StartX=318.073 StartY=-69.424 StartZ=0 EndX=318.073 EndY=-87.7794 EndZ=0
    g284: LineSegment StartX=322.073 StartY=-91.7794 StartZ=0 EndX=362.073 EndY=-91.7794 EndZ=0
    g285: Circle CenterX=2.07281 CenterY=124.221 CenterZ=0 NormalX=0 NormalY=0 NormalZ=1 AngleXU=0 Radius=1
    g286: Circle CenterX=1.57905 CenterY=122.295 CenterZ=0 NormalX=0 NormalY=0 NormalZ=1 AngleXU=0 Radius=1
    g287: BSplineCurve PolesCount=3 KnotsCount=2 Degree=2 IsPeriodic=0
    g288: GeomPoint X=2.07281 Y=124.221 Z=0
    g289: GeomPoint X=1.57905 Y=122.295 Z=0
    g290: Circle CenterX=42.0728 CenterY=124.221 CenterZ=0 NormalX=0 NormalY=0 NormalZ=1 AngleXU=0 Radius=1
    g291: Circle CenterX=46.0728 CenterY=124.221 CenterZ=0 NormalX=0 NormalY=0 NormalZ=1 AngleXU=0 Radius=1
    g292: Circle CenterX=46.0728 CenterY=120.221 CenterZ=0 NormalX=0 NormalY=0 NormalZ=1 AngleXU=0 Radius=1
    g293: BSplineCurve PolesCount=3 KnotsCount=2 Degree=2 IsPeriodic=0
    g294: GeomPoint X=42.0728 Y=124.221 Z=0
    g295: GeomPoint X=46.0728 Y=120.221 Z=0
    g296: Circle CenterX=46.0728 CenterY=109.865 CenterZ=0 NormalX=0 NormalY=0 NormalZ=1 AngleXU=0 Radius=1
    g297: Circle CenterX=46.0728 CenterY=105.865 CenterZ=0 NormalX=0 NormalY=0 NormalZ=1 AngleXU=0 Radius=1
    g298: Circle CenterX=42.0728 CenterY=105.865 CenterZ=0 NormalX=0 NormalY=0 NormalZ=1 AngleXU=0 Radius=1
    g299: BSplineCurve PolesCount=3 KnotsCount=2 Degree=2 IsPeriodic=0
    g300: GeomPoint X=46.0728 Y=109.865 Z=0
    g301: GeomPoint X=42.0728 Y=105.865 Z=0
    g302: Circle CenterX=35.5028 CenterY=105.865 CenterZ=0 NormalX=0 NormalY=0 NormalZ=1 AngleXU=0 Radius=1
    g303: Circle CenterX=31.5028 CenterY=105.865 CenterZ=0 NormalX=0 NormalY=0 NormalZ=1 AngleXU=0 Radius=1
    g304: Circle CenterX=27.9965 CenterY=107.79 CenterZ=0 NormalX=0 NormalY=0 NormalZ=1 AngleXU=0 Radius=1
    g305: BSplineCurve PolesCount=3 KnotsCount=2 Degree=2 IsPeriodic=0
    g306: GeomPoint X=35.5028 Y=105.865 Z=0
    g307: GeomPoint X=27.9965 Y=107.79 Z=0
    g308: LineSegment StartX=2.07281 StartY=124.221 StartZ=0 EndX=42.0728 EndY=124.221 EndZ=0
    g309: LineSegment StartX=46.0728 StartY=120.221 StartZ=0 EndX=46.0728 EndY=109.865 EndZ=0
    g310: LineSegment StartX=42.0728 StartY=105.865 StartZ=0 EndX=35.5028 EndY=105.865 EndZ=0
    g311: LineSegment StartX=27.9965 StartY=107.79 StartZ=0 EndX=1.57905 EndY=122.295 EndZ=0
    g312: Circle CenterX=42.5666 CenterY=-67.3492 CenterZ=0 NormalX=0 NormalY=0 NormalZ=1 AngleXU=0 Radius=1
    g313: Circle CenterX=46.0728 CenterY=-65.424 CenterZ=0 NormalX=0 NormalY=0 NormalZ=1 AngleXU=0 Radius=1
    g314: Circle CenterX=46.0728 CenterY=-69.424 CenterZ=0 NormalX=0 NormalY=0 NormalZ=1 AngleXU=0 Radius=1
    g315: BSplineCurve PolesCount=3 KnotsCount=2 Degree=2 IsPeriodic=0
    g316: GeomPoint X=42.5666 Y=-67.3492 Z=0
    g317: GeomPoint X=46.0728 Y=-69.424 Z=0
    g318: Circle CenterX=46.0728 CenterY=-87.7794 CenterZ=0 NormalX=0 NormalY=0 NormalZ=1 AngleXU=0 Radius=1
    g319: Circle CenterX=46.0728 CenterY=-91.7794 CenterZ=0 NormalX=0 NormalY=0 NormalZ=1 AngleXU=0 Radius=1
    g320: Circle CenterX=42.0728 CenterY=-91.7794 CenterZ=0 NormalX=0 NormalY=0 NormalZ=1 AngleXU=0 Radius=1
    g321: BSplineCurve PolesCount=3 KnotsCount=2 Degree=2 IsPeriodic=0
    g322: GeomPoint X=46.0728 Y=-87.7794 Z=0
    g323: GeomPoint X=42.0728 Y=-91.7794 Z=0
    g324: Circle CenterX=2.07281 CenterY=-91.7794 CenterZ=0 NormalX=0 NormalY=0 NormalZ=1 AngleXU=0 Radius=1
    g325: Circle CenterX=-1.92719 CenterY=-91.7794 CenterZ=0 NormalX=0 NormalY=0 NormalZ=1 AngleXU=0 Radius=1
    g326: Circle CenterX=1.57905 CenterY=-89.8542 CenterZ=0 NormalX=0 NormalY=0 NormalZ=1 AngleXU=0 Radius=1
    g327: BSplineCurve PolesCount=3 KnotsCount=2 Degree=2 IsPeriodic=0
    g328: GeomPoint X=2.07281 Y=-91.7794 Z=0
    g329: GeomPoint X=1.57905 Y=-89.8542 Z=0
    g330: LineSegment StartX=2.07281 StartY=-91.7794 StartZ=0 EndX=42.0728 EndY=-91.7794 EndZ=0
    g331: LineSegment StartX=46.0728 StartY=-87.7794 StartZ=0 EndX=46.0728 EndY=-69.424 EndZ=0
    g332: LineSegment StartX=42.5666 StartY=-67.3492 StartZ=0 EndX=1.57905 EndY=-89.8542 EndZ=0
    g333: Circle CenterX=322.073 CenterY=76.4095 CenterZ=0 NormalX=0 NormalY=0 NormalZ=1 AngleXU=0 Radius=4
    g334: BSplineCurve PolesCount=3 KnotsCount=2 Degree=2 IsPeriodic=0
    g335: GeomPoint X=318.073 Y=72.4095 Z=0
    g336: GeomPoint X=322.073 Y=76.4095 Z=0
    g337: Circle CenterX=375.073 CenterY=72.4095 CenterZ=0 NormalX=0 NormalY=0 NormalZ=1 AngleXU=0 Radius=1
    g338: Circle CenterX=375.073 CenterY=76.4095 CenterZ=0 NormalX=0 NormalY=0 NormalZ=1 AngleXU=0 Radius=1
    g339: Circle CenterX=371.073 CenterY=76.4095 CenterZ=0 NormalX=0 NormalY=0 NormalZ=1 AngleXU=0 Radius=1
    g340: BSplineCurve PolesCount=3 KnotsCount=2 Degree=2 IsPeriodic=0
    g341: GeomPoint X=375.073 Y=72.4095 Z=0
    g342: GeomPoint X=371.073 Y=76.4095 Z=0
    g343: LineSegment StartX=322.073 StartY=76.4095 StartZ=0 EndX=371.073 EndY=76.4095 EndZ=0
    g344: LineSegment StartX=318.073 StartY=72.4095 StartZ=0 EndX=318.073 EndY=-47.4805 EndZ=0
    g345: LineSegment StartX=375.073 StartY=72.4095 StartZ=0 EndX=375.073 EndY=-78.7896 EndZ=0
    g346: ArcOfCircle CenterX=-26.9272 CenterY=22.1087 CenterZ=0 NormalX=0 NormalY=0 NormalZ=1 AngleXU=0 Radius=4 StartAngle=5e-16 EndAngle=3.14159
    g347: LineSegment StartX=-30.9272 StartY=22.1087 StartZ=0 EndX=-34.9272 EndY=-83.7794 EndZ=0
    g348: LineSegment StartX=-18.9272 StartY=-83.7794 StartZ=0 EndX=-22.9272 EndY=22.1087 EndZ=0
  constraints (572):
    c: Coincident(g0,g2)
    c: Block(g0)
    c: Block(g1)
    c: Vertical(g3)
    c: Vertical(g4)
    c: Block(g4)
    c: Block(g3)
    c: Tangent(g6,g7) = 1.5708
    c: Tangent(g7,g9) = 1.5708
    c: Equal(g6,g9)
    c: Coincident(g8,g6)
    c: Coincident(g8,g9)
    c: Block(g7)
    c: Block(g8)
    c: Weight(g10) = 1
    c: Equal(g10,g11)
    c: Equal(g10,g12)
    c: InternalAlignment(g10,g13)
    c: InternalAlignment(g11,g13)
    c: InternalAlignment(g12,g13)
    c: InternalAlignment(g14,g13)
    c: InternalAlignment(g15,g13)
    c: Weight(g16) = 1
    c: Equal(g16,g17)
    c: Equal(g16,g18)
    c: InternalAlignment(g16,g19)
    c: InternalAlignment(g17,g19)
    c: InternalAlignment(g18,g19)
    c: InternalAlignment(g20,g19)
    c: InternalAlignment(g21,g19)
    c: Block(g19)
    c: Block(g13)
    c: Weight(g22) = 1
    c: Equal(g22,g23)
    c: Equal(g22,g24)
    c: InternalAlignment(g22,g25)
    c: InternalAlignment(g23,g25)
    c: InternalAlignment(g24,g25)
    c: InternalAlignment(g26,g25)
    c: InternalAlignment(g27,g25)
    c: Weight(g28) = 1
    c: Equal(g28,g29)
    c: Equal(g28,g30)
    c: InternalAlignment(g28,g31)
    c: InternalAlignment(g29,g31)
    c: InternalAlignment(g30,g31)
    c: InternalAlignment(g32,g31)
    c: InternalAlignment(g33,g31)
    c: Block(g31)
    c: Block(g25)
    c: Weight(g34) = 1
    c: Equal(g34,g35)
    c: Equal(g34,g36)
    c: InternalAlignment(g34,g37)
    c: InternalAlignment(g35,g37)
    c: InternalAlignment(g36,g37)
    c: InternalAlignment(g38,g37)
    c: InternalAlignment(g39,g37)
    c: Weight(g40) = 1
    c: Equal(g40,g41)
    c: Equal(g40,g42)
    c: InternalAlignment(g40,g43)
    c: InternalAlignment(g41,g43)
    c: InternalAlignment(g42,g43)
    c: InternalAlignment(g44,g43)
    c: InternalAlignment(g45,g43)
    c: Block(g37)
    c: Block(g43)
    c: Coincident(g46,g4)
    c: Coincident(g46,g3)
    c: Horizontal(g46)
    c: Distance(g46) = 450
    c: Coincident(g47,g4)
    c: Coincident(g47,g3)
    c: Horizontal(g47)
    c: Horizontal(g48)
    c: Coincident(g2,g48)
    c: Block(g48)
    c: Coincident(g1,g48)
    c: Weight(g49) = 1
    c: Equal(g49,g50)
    c: Equal(g49,g51)
    c: InternalAlignment(g49,g52)
    c: InternalAlignment(g50,g52)
    c: InternalAlignment(g51,g52)
    c: InternalAlignment(g53,g52)
    c: InternalAlignment(g54,g52)
    c: Block(g52)
    c: Weight(g55) = 1
    c: Equal(g55,g56)
    c: Equal(g55,g57)
    c: InternalAlignment(g55,g58)
    c: InternalAlignment(g56,g58)
    c: InternalAlignment(g57,g58)
    c: InternalAlignment(g59,g58)
    c: InternalAlignment(g60,g58)
    c: Block(g58)
    c: Weight(g61) = 1
    c: Equal(g61,g62)
    c: Equal(g61,g63)
    c: InternalAlignment(g61,g64)
    c: InternalAlignment(g62,g64)
    c: InternalAlignment(g63,g64)
    c: InternalAlignment(g65,g64)
    c: InternalAlignment(g66,g64)
    c: Block(g64)
    c: Weight(g67) = 1
    c: Equal(g67,g68)
    c: Equal(g67,g69)
    c: InternalAlignment(g67,g70)
    c: InternalAlignment(g68,g70)
    c: InternalAlignment(g69,g70)
    c: InternalAlignment(g71,g70)
    c: InternalAlignment(g72,g70)
    c: Block(g70)
    c: Weight(g73) = 1
    c: Equal(g73,g74)
    c: Equal(g73,g75)
    c: InternalAlignment(g73,g76)
    c: InternalAlignment(g74,g76)
    c: InternalAlignment(g75,g76)
    c: InternalAlignment(g77,g76)
    c: InternalAlignment(g78,g76)
    c: Weight(g79) = 1
    c: Equal(g79,g80)
    c: Equal(g79,g81)
    c: InternalAlignment(g79,g82)
    c: InternalAlignment(g80,g82)
    c: InternalAlignment(g81,g82)
    c: InternalAlignment(g83,g82)
    c: InternalAlignment(g84,g82)
    c: Block(g76)
    c: Block(g82)
    c: Coincident(g85,g76)
    c: Coincident(g85,g82)
    c: Vertical(g85)
    c: Coincident(g86,g76)
    c: Coincident(g86,g58)
    c: Coincident(g87,g58)
    c: Coincident(g87,g82)
    c: Weight(g88) = 1
    c: Equal(g88,g89)
    c: Equal(g88,g90)
    c: InternalAlignment(g88,g91)
    c: InternalAlignment(g89,g91)
    c: InternalAlignment(g90,g91)
    c: InternalAlignment(g92,g91)
    c: InternalAlignment(g93,g91)
    c: Weight(g94) = 1
    c: Equal(g94,g95)
    c: Equal(g94,g96)
    c: InternalAlignment(g94,g97)
    c: InternalAlignment(g95,g97)
    c: InternalAlignment(g96,g97)
    c: InternalAlignment(g98,g97)
    c: InternalAlignment(g99,g97)
    c: Block(g91)
    c: Block(g97)
    c: Coincident(g100,g91)
    c: Coincident(g100,g97)
    c: Vertical(g100)
    c: Coincident(g101,g91)
    c: Coincident(g101,g52)
    c: Coincident(g102,g52)
    c: Coincident(g102,g97)
    c: Weight(g103) = 1
    c: Equal(g103,g104)
    c: Equal(g103,g105)
    c: InternalAlignment(g103,g106)
    c: InternalAlignment(g104,g106)
    c: InternalAlignment(g105,g106)
    c: InternalAlignment(g107,g106)
    c: InternalAlignment(g108,g106)
    c: Weight(g109) = 1
    c: Equal(g109,g110)
    c: Equal(g109,g111)
    c: InternalAlignment(g109,g112)
    c: InternalAlignment(g110,g112)
    c: InternalAlignment(g111,g112)
    c: InternalAlignment(g113,g112)
    c: InternalAlignment(g114,g112)
    c: Block(g106)
    c: Block(g112)
    c: Coincident(g115,g106)
    c: Coincident(g115,g112)
    c: Vertical(g115)
    c: Coincident(g116,g112)
    c: Coincident(g116,g70)
    c: Coincident(g117,g70)
    c: Coincident(g117,g106)
    c: Weight(g118) = 1
    c: Equal(g118,g119)
    c: Equal(g118,g120)
    c: InternalAlignment(g118,g121)
    c: InternalAlignment(g119,g121)
    c: InternalAlignment(g120,g121)
    c: InternalAlignment(g122,g121)
    c: InternalAlignment(g123,g121)
    c: Weight(g124) = 1
    c: Equal(g124,g125)
    c: Equal(g124,g126)
    c: InternalAlignment(g124,g127)
    c: InternalAlignment(g125,g127)
    c: InternalAlignment(g126,g127)
    c: InternalAlignment(g128,g127)
    c: InternalAlignment(g129,g127)
    c: Block(g121)
    c: Block(g127)
    c: Coincident(g130,g121)
    c: Coincident(g130,g127)
    c: Vertical(g130)
    c: Coincident(g131,g127)
    c: Coincident(g131,g64)
    c: Coincident(g132,g64)
    c: Coincident(g132,g121)
    c: Weight(g133) = 1
    c: Equal(g133,g134)
    c: Equal(g133,g135)
    c: InternalAlignment(g133,g136)
    c: InternalAlignment(g134,g136)
    c: InternalAlignment(g135,g136)
    c: InternalAlignment(g137,g136)
    c: InternalAlignment(g138,g136)
    c: Weight(g139) = 1
    c: Equal(g139,g140)
    c: Equal(g139,g141)
    c: InternalAlignment(g139,g142)
    c: InternalAlignment(g140,g142)
    c: InternalAlignment(g141,g142)
    c: InternalAlignment(g143,g142)
    c: InternalAlignment(g144,g142)
    c: Weight(g145) = 1
    c: Equal(g145,g146)
    c: Equal(g145,g147)
    c: InternalAlignment(g145,g148)
    c: InternalAlignment(g146,g148)
    c: InternalAlignment(g147,g148)
    c: InternalAlignment(g149,g148)
    c: InternalAlignment(g150,g148)
    c: Weight(g151) = 1
    c: Equal(g151,g152)
    c: Equal(g151,g153)
    c: InternalAlignment(g151,g154)
    c: InternalAlignment(g152,g154)
    c: InternalAlignment(g153,g154)
    c: InternalAlignment(g155,g154)
    c: InternalAlignment(g156,g154)
    c: Block(g154)
    c: Block(g148)
    c: Block(g142)
    c: Block(g136)
    c: Coincident(g157,g31)
    c: Coincident(g157,g154)
    c: Coincident(g158,g154)
    c: Coincident(g158,g148)
    c: Horizontal(g158)
    c: Coincident(g159,g148)
    c: Coincident(g159,g31)
    c: Vertical(g159)
    c: Coincident(g160,g25)
    c: Coincident(g160,g142)
    c: Vertical(g160)
    c: Coincident(g161,g142)
    c: Coincident(g161,g136)
    c: Horizontal(g161)
    c: Coincident(g162,g136)
    c: Coincident(g162,g25)
    c: Weight(g163) = 1
    c: Equal(g163,g164)
    c: Equal(g163,g165)
    c: InternalAlignment(g163,g166)
    c: InternalAlignment(g164,g166)
    c: InternalAlignment(g165,g166)
    c: InternalAlignment(g167,g166)
    c: InternalAlignment(g168,g166)
    c: Weight(g169) = 1
    c: Equal(g169,g170)
    c: Equal(g169,g171)
    c: InternalAlignment(g169,g172)
    c: InternalAlignment(g170,g172)
    c: InternalAlignment(g171,g172)
    c: InternalAlignment(g173,g172)
    c: InternalAlignment(g174,g172)
    c: Weight(g175) = 1
    c: Equal(g175,g176)
    c: Equal(g175,g177)
    c: InternalAlignment(g175,g178)
    c: InternalAlignment(g176,g178)
    c: InternalAlignment(g177,g178)
    c: InternalAlignment(g179,g178)
    c: InternalAlignment(g180,g178)
    c: Weight(g181) = 1
    c: Equal(g181,g182)
    c: Equal(g181,g183)
    c: InternalAlignment(g181,g184)
    c: InternalAlignment(g182,g184)
    c: InternalAlignment(g183,g184)
    c: InternalAlignment(g185,g184)
    c: InternalAlignment(g186,g184)
    c: Block(g184)
    c: Block(g178)
    c: Block(g172)
    c: Block(g166)
    c: Coincident(g187,g184)
    c: Coincident(g187,g178)
    c: Horizontal(g187)
    c: Coincident(g188,g178)
    c: Coincident(g188,g13)
    c: Vertical(g188)
    c: Coincident(g189,g19)
    c: Coincident(g189,g172)
    c: Vertical(g189)
    c: Coincident(g190,g172)
    c: Coincident(g190,g166)
    c: Horizontal(g190)
    c: Coincident(g191,g166)
    c: Coincident(g191,g19)
    c: Coincident(g192,g13)
    c: Weight(g193) = 1
    c: Equal(g193,g194)
    c: Equal(g193,g195)
    c: InternalAlignment(g193,g196)
    c: InternalAlignment(g194,g196)
    c: InternalAlignment(g195,g196)
    c: InternalAlignment(g197,g196)
    c: InternalAlignment(g198,g196)
    c: Weight(g199) = 1
    c: Equal(g199,g200)
    c: Equal(g199,g201)
    c: InternalAlignment(g199,g202)
    c: InternalAlignment(g200,g202)
    c: InternalAlignment(g201,g202)
    c: InternalAlignment(g203,g202)
    c: InternalAlignment(g204,g202)
    c: Block(g202)
    c: Block(g196)
    c: Coincident(g205,g202)
    c: Coincident(g205,g37)
    c: Coincident(g206,g37)
    c: Coincident(g206,g196)
    c: Coincident(g207,g196)
    c: Coincident(g207,g202)
    c: Vertical(g207)
    c: Weight(g208) = 1
    c: Equal(g208,g209)
    c: Equal(g208,g210)
    c: InternalAlignment(g208,g211)
    c: InternalAlignment(g209,g211)
    c: InternalAlignment(g210,g211)
    c: InternalAlignment(g212,g211)
    c: InternalAlignment(g213,g211)
    c: Weight(g214) = 1
    c: Equal(g214,g215)
    c: Equal(g214,g216)
    c: InternalAlignment(g214,g217)
    c: InternalAlignment(g215,g217)
    c: InternalAlignment(g216,g217)
    c: InternalAlignment(g218,g217)
    c: InternalAlignment(g219,g217)
    c: Block(g217)
    c: Block(g211)
    c: Coincident(g220,g211)
    c: Coincident(g220,g43)
    c: Coincident(g221,g43)
    c: Coincident(g221,g217)
    c: Coincident(g222,g217)
    c: Coincident(g222,g211)
    c: Vertical(g222)
    c: Horizontal(g223)
    c: Block(g223)
    c: Vertical(g224)
    c: Block(g224)
    c: Block(g225)
    c: Weight(g226) = 1
    c: Equal(g226,g227)
    c: Equal(g226,g228)
    c: InternalAlignment(g226,g229)
    c: InternalAlignment(g227,g229)
    c: InternalAlignment(g228,g229)
    c: InternalAlignment(g230,g229)
    c: InternalAlignment(g231,g229)
    c: Weight(g232) = 1
    c: Equal(g232,g233)
    c: Equal(g232,g234)
    c: InternalAlignment(g232,g235)
    c: InternalAlignment(g233,g235)
    c: InternalAlignment(g234,g235)
    c: InternalAlignment(g236,g235)
    c: InternalAlignment(g237,g235)
    c: Weight(g238) = 1
    c: Equal(g238,g239)
    c: Equal(g238,g240)
    c: InternalAlignment(g238,g241)
    c: InternalAlignment(g239,g241)
    c: InternalAlignment(g240,g241)
    c: InternalAlignment(g242,g241)
    c: InternalAlignment(g243,g241)
    c: Weight(g244) = 1
    c: Equal(g244,g245)
    c: Equal(g244,g246)
    c: InternalAlignment(g244,g247)
    c: InternalAlignment(g245,g247)
    c: InternalAlignment(g246,g247)
    c: InternalAlignment(g248,g247)
    c: InternalAlignment(g249,g247)
    c: Block(g229)
    c: Block(g235)
    c: Block(g241)
    c: Block(g247)
    c: Coincident(g250,g235)
    c: Coincident(g250,g229)
    c: Horizontal(g250)
    c: Block(g192)
    c: Weight(g251) = 1
    c: Equal(g251,g252)
    c: Equal(g251,g253)
    c: InternalAlignment(g251,g254)
    c: InternalAlignment(g252,g254)
    c: InternalAlignment(g253,g254)
    c: InternalAlignment(g255,g254)
    c: InternalAlignment(g256,g254)
    c: Weight(g257) = 1
    c: Equal(g257,g258)
    c: Equal(g257,g259)
    c: InternalAlignment(g257,g260)
    c: InternalAlignment(g258,g260)
    c: InternalAlignment(g259,g260)
    c: InternalAlignment(g261,g260)
    c: InternalAlignment(g262,g260)
    c: Block(g254)
    c: Block(g260)
    c: Coincident(g263,g254)
    c: Coincident(g263,g260)
    c: Weight(g264) = 1
    c: Equal(g264,g265)
    c: Equal(g264,g266)
    c: InternalAlignment(g264,g267)
    c: InternalAlignment(g265,g267)
    c: InternalAlignment(g266,g267)
    c: InternalAlignment(g268,g267)
    c: InternalAlignment(g269,g267)
    c: Weight(g270) = 1
    c: Equal(g270,g271)
    c: Equal(g270,g272)
    c: InternalAlignment(g270,g273)
    c: InternalAlignment(g271,g273)
    c: InternalAlignment(g272,g273)
    c: InternalAlignment(g274,g273)
    c: InternalAlignment(g275,g273)
    c: Weight(g276) = 1
    c: Equal(g276,g277)
    c: Equal(g276,g278)
    c: InternalAlignment(g276,g279)
    c: InternalAlignment(g277,g279)
    c: InternalAlignment(g278,g279)
    c: InternalAlignment(g280,g279)
    c: InternalAlignment(g281,g279)
    c: Block(g279)
    c: Block(g273)
    c: Block(g267)
    c: Coincident(g282,g273)
    c: Coincident(g282,g267)
    c: Coincident(g283,g267)
    c: Coincident(g283,g279)
    c: Vertical(g283)
    c: Coincident(g284,g279)
    c: Coincident(g284,g273)
    c: Horizontal(g284)
    c: Weight(g285) = 1
    c: Equal(g285,g286)
    c: InternalAlignment(g285,g287)
    c: InternalAlignment(g286,g287)
    c: InternalAlignment(g288,g287)
    c: InternalAlignment(g289,g287)
    c: Weight(g290) = 1
    c: InternalAlignment(g291,g293)
    c: InternalAlignment(g292,g293)
    c: InternalAlignment(g294,g293)
    c: InternalAlignment(g295,g293)
    c: Weight(g296) = 1
    c: Equal(g296,g297)
    c: Equal(g296,g298)
    c: InternalAlignment(g296,g299)
    c: InternalAlignment(g297,g299)
    c: InternalAlignment(g298,g299)
    c: InternalAlignment(g300,g299)
    c: InternalAlignment(g301,g299)
    c: Equal(g302,g303)
    c: Equal(g302,g304)
    c: InternalAlignment(g302,g305)
    c: InternalAlignment(g303,g305)
    c: InternalAlignment(g304,g305)
    c: InternalAlignment(g306,g305)
    c: InternalAlignment(g307,g305)
    c: Block(g293)
    c: Block(g299)
    c: Block(g305)
    c: Block(g287)
    c: Coincident(g308,g287)
    c: Coincident(g308,g293)
    c: Horizontal(g308)
    c: Coincident(g309,g293)
    c: Coincident(g309,g299)
    c: Vertical(g309)
    c: Coincident(g310,g299)
    c: Coincident(g310,g305)
    c: Horizontal(g310)
    c: Coincident(g311,g305)
    c: Coincident(g311,g287)
    c: Weight(g312) = 1
    c: Equal(g312,g313)
    c: Equal(g312,g314)
    c: InternalAlignment(g312,g315)
    c: InternalAlignment(g313,g315)
    c: InternalAlignment(g314,g315)
    c: InternalAlignment(g316,g315)
    c: InternalAlignment(g317,g315)
    c: Weight(g318) = 1
    c: Equal(g318,g319)
    c: Equal(g318,g320)
    c: InternalAlignment(g318,g321)
    c: InternalAlignment(g319,g321)
    c: InternalAlignment(g320,g321)
    c: InternalAlignment(g322,g321)
    c: InternalAlignment(g323,g321)
    c: Weight(g324) = 1
    c: Equal(g324,g325)
    c: Equal(g324,g326)
    c: InternalAlignment(g324,g327)
    c: InternalAlignment(g325,g327)
    c: InternalAlignment(g326,g327)
    c: InternalAlignment(g328,g327)
    c: InternalAlignment(g329,g327)
    c: Block(g327)
    c: Block(g321)
    c: Block(g315)
    c: Coincident(g330,g327)
    c: Coincident(g330,g321)
    c: Horizontal(g330)
    c: Coincident(g331,g321)
    c: Coincident(g331,g315)
    c: Vertical(g331)
    c: Coincident(g332,g315)
    c: Coincident(g332,g327)
    c: InternalAlignment(g333,g334)
    c: InternalAlignment(g335,g334)
    c: InternalAlignment(g336,g334)
    c: Block(g334)
    c: Equal(g337,g338)
    c: Equal(g337,g339)
    c: InternalAlignment(g337,g340)
    c: InternalAlignment(g338,g340)
    c: InternalAlignment(g339,g340)
    c: InternalAlignment(g341,g340)
    c: InternalAlignment(g342,g340)
    c: Block(g340)
    c: Coincident(g343,g334)
    c: Horizontal(g343)
    c: Block(g343)
    c: Coincident(g344,g334)
    c: Coincident(g344,g260)
    c: Vertical(g344)
    c: Coincident(g345,g340)
    c: Coincident(g345,g254)
    c: Vertical(g345)
    c: Coincident(g347,g5)
    c: Coincident(g348,g5)
    c: Block(g346)
    c: Block(g5)
    c: Block(g348)
    c: Block(g347)
    c: Distance(g344) = 119.89
FEATURE [Sketcher::SketchObject] Sketch001
  FullyConstrained = true
  MapMode = 4
  Placement = pos=(0,0,0) rot=(0.57735,0.57735,0.57735;2.0944rad)
  Support = -> [Sketch]
  sketch-geometry (46):
    g0: BSplineCurve PolesCount=3 KnotsCount=2 Degree=2 IsPeriodic=0
    g1: ArcOfCircle CenterX=73.1223 CenterY=-32.291 CenterZ=0 NormalX=0 NormalY=0 NormalZ=1 AngleXU=0 Radius=13 StartAngle=5.92268 EndAngle=9.06428
    g2: ArcOfCircle CenterX=66.7816 CenterY=-49.1439 CenterZ=0 NormalX=0 NormalY=0 NormalZ=1 AngleXU=0 Radius=13 StartAngle=2.78068 EndAngle=5.92131
    g3: ArcOfCircle CenterX=55.9263 CenterY=-78.1807 CenterZ=0 NormalX=0 NormalY=0 NormalZ=1 AngleXU=0 Radius=13 StartAngle=5.92268 EndAngle=9.06428
    g4: ArcOfCircle CenterX=49.5884 CenterY=-95.0342 CenterZ=0 NormalX=0 NormalY=0 NormalZ=1 AngleXU=0 Radius=13 StartAngle=2.78068 EndAngle=5.92131
    g5: ArcOfCircle CenterX=38.7206 CenterY=-124.067 CenterZ=0 NormalX=0 NormalY=0 NormalZ=1 AngleXU=0 Radius=13 StartAngle=5.92268 EndAngle=9.06428
    g6: ArcOfCircle CenterX=32.3875 CenterY=-140.92 CenterZ=0 NormalX=0 NormalY=0 NormalZ=1 AngleXU=0 Radius=13 StartAngle=2.78068 EndAngle=5.92131
    g7: ArcOfCircle CenterX=21.4715 CenterY=-169.934 CenterZ=0 NormalX=0 NormalY=0 NormalZ=1 AngleXU=0 Radius=13 StartAngle=5.92268 EndAngle=9.06428
    g8: ArcOfCircle CenterX=15.1336 CenterY=-186.787 CenterZ=0 NormalX=0 NormalY=0 NormalZ=1 AngleXU=0 Radius=13 StartAngle=2.78068 EndAngle=5.92131
    g9-g12: Circle x4 (B-spline internal-alignment scaffolding for g13; pole/knot coordinates omitted)
    g13: BSplineCurve PolesCount=4 KnotsCount=2 Degree=3 IsPeriodic=0
    g14: GeomPoint X=28.8094 Y=-19.0875 Z=0
    g15: GeomPoint X=47.0443 Y=-50.4712 Z=0
    g16: Circle CenterX=53.5586 CenterY=-23.2695 CenterZ=0 NormalX=0 NormalY=0 NormalZ=1 AngleXU=0 Radius=3.24518
    g17: Circle CenterX=-195.441 CenterY=-127.082 CenterZ=0 NormalX=0 NormalY=0 NormalZ=1 AngleXU=0 Radius=1
    g18: Circle CenterX=-8.24091 CenterY=-197.481 CenterZ=0 NormalX=0 NormalY=0 NormalZ=1 AngleXU=0 Radius=1
    g19: Circle CenterX=12.8789 CenterY=-141.321 CenterZ=0 NormalX=0 NormalY=0 NormalZ=1 AngleXU=0 Radius=1
    g20: BSplineCurve PolesCount=3 KnotsCount=2 Degree=2 IsPeriodic=0
    g21: GeomPoint X=-195.441 Y=-127.082 Z=0
    g22: GeomPoint X=12.8789 Y=-141.321 Z=0
    g23: Circle CenterX=-12.8016 CenterY=-179.036 CenterZ=0 NormalX=0 NormalY=0 NormalZ=1 AngleXU=0 Radius=10.5072
    g24: Circle CenterX=0.933922 CenterY=-166.43 CenterZ=0 NormalX=0 NormalY=0 NormalZ=1 AngleXU=0 Radius=3.26661
    g25: Circle CenterX=-33.5518 CenterY=-176.44 CenterZ=0 NormalX=0 NormalY=0 NormalZ=1 AngleXU=0 Radius=5.64388
    g26: Circle CenterX=-47.2366 CenterY=-173.859 CenterZ=0 NormalX=0 NormalY=0 NormalZ=1 AngleXU=0 Radius=3.01653
    g27: Circle CenterX=-56.2595 CenterY=-171.456 CenterZ=0 NormalX=0 NormalY=0 NormalZ=1 AngleXU=0 Radius=2.12826
    g28: ArcOfCircle CenterX=51.2151 CenterY=-198.473 CenterZ=0 NormalX=0 NormalY=0 NormalZ=1 AngleXU=0 Radius=20 StartAngle=2.78189 EndAngle=4.35269
    g29: LineSegment StartX=32.4951 StartY=-191.433 StartZ=0 EndX=94.6578 EndY=-26.1352 EndZ=0
    g30: LineSegment StartX=43.1192 StartY=-220.001 StartZ=0 EndX=-196.497 EndY=-129.89 EndZ=0
    g31: LineSegment StartX=43.1192 StartY=-220.001 StartZ=0 EndX=44.1752 EndY=-217.193 EndZ=0
    g32: LineSegment StartX=117.223 StartY=-19.0875 StartZ=0 EndX=117.223 EndY=-16.0875 EndZ=0
    g33: LineSegment StartX=117.223 StartY=-16.0875 StartZ=0 EndX=17.2232 EndY=-16.0875 EndZ=0
    g34: LineSegment StartX=17.2232 StartY=-16.0875 StartZ=0 EndX=17.2232 EndY=-19.0875 EndZ=0
    g35: LineSegment StartX=28.8094 StartY=-19.0875 StartZ=0 EndX=17.2232 EndY=-19.0875 EndZ=0
    g36: LineSegment StartX=47.0443 StartY=-50.4712 StartZ=0 EndX=12.8789 EndY=-141.321 EndZ=0
    g37: LineSegment StartX=-195.441 StartY=-127.082 StartZ=0 EndX=-196.497 EndY=-129.89 EndZ=0
    g38: LineSegment StartX=85.2866 StartY=-36.8766 StartZ=0 EndX=78.9396 EndY=-53.7463 EndZ=0
    g39: LineSegment StartX=60.9579 StartY=-27.7053 StartZ=0 EndX=54.6191 EndY=-44.5532 EndZ=0
    g40: LineSegment StartX=68.0907 StartY=-82.7664 StartZ=0 EndX=61.7465 EndY=-99.6365 EndZ=0
    g41: LineSegment StartX=43.7619 StartY=-73.595 StartZ=0 EndX=37.426 EndY=-90.4435 EndZ=0
    g42: LineSegment StartX=50.885 StartY=-128.652 StartZ=0 EndX=44.5456 EndY=-145.522 EndZ=0
    g43: LineSegment StartX=26.5562 StartY=-119.481 StartZ=0 EndX=20.2251 EndY=-136.329 EndZ=0
    g44: LineSegment StartX=9.3071 StartY=-165.349 StartZ=0 EndX=2.97115 EndY=-182.197 EndZ=0
    g45: LineSegment StartX=33.6358 StartY=-174.52 StartZ=0 EndX=27.2917 EndY=-191.39 EndZ=0
  constraints (71):
    c: Block(g0)
    c: Block(g1)
    c: Block(g2)
    c: Block(g4)
    c: Block(g3)
    c: Block(g6)
    c: Block(g5)
    c: Block(g8)
    c: Block(g7)
    c: Weight(g9) = 1
    c: Equal(g9,g10)
    c: Equal(g9,g11)
    c: Equal(g9,g12)
    c: InternalAlignment(g9-g12 -> g13) x4
    c: InternalAlignment(g14,g13)
    c: InternalAlignment(g15,g13)
    c: Block(g16)
    c: Weight(g17) = 1
    c: Equal(g17,g18)
    c: Equal(g17,g19)
    c: InternalAlignment(g17,g20)
    c: InternalAlignment(g18,g20)
    c: InternalAlignment(g19,g20)
    c: InternalAlignment(g21,g20)
    c: InternalAlignment(g22,g20)
    c: Block(g20)
    c: Block(g23)
    c: Block(g24)
    c: Block(g25)
    c: Block(g26)
    c: Block(g27)
    c: Block(g28)
    c: Coincident(g29,g28)
    c: Coincident(g29,g0)
    c: Block(g13)
    c: Coincident(g31,g30)
    c: Coincident(g31,g28)
    c: Block(g31)
    c: Coincident(g32,g0)
    c: Vertical(g32)
    c: Coincident(g33,g32)
    c: Horizontal(g33)
    c: Coincident(g34,g33)
    c: Vertical(g34)
    c: Block(g33)
    c: Coincident(g35,g13)
    c: Coincident(g35,g34)
    c: Horizontal(g35)
    c: Coincident(g36,g13)
    c: Coincident(g36,g20)
    c: Coincident(g37,g20)
    c: Coincident(g37,g30)
    c: Block(g30)
    c: Coincident(g38,g1)
    c: Coincident(g38,g2)
    c: Coincident(g39,g1)
    c: Coincident(g39,g2)
    c: Coincident(g40,g3)
    c: Coincident(g40,g4)
    c: Coincident(g41,g3)
    c: Coincident(g41,g4)
    c: Coincident(g42,g5)
    c: Coincident(g42,g6)
    c: Coincident(g43,g5)
    c: Coincident(g43,g6)
    c: Coincident(g44,g7)
    c: Coincident(g44,g8)
    c: Coincident(g45,g7)
    c: Coincident(g45,g8)
    c: Distance(g30) = 256
    c: Distance(g33) = 100
FEATURE [Part::Extrusion] Extrude002
  Base = -> Sketch001
  Dir = (1,0,0)
  DirMode = 2
  FaceMakerClass = Part::FaceMakerBullseye
  LengthFwd = 8
  LengthRev = 0
  Solid = true
  Symmetric = false
FEATURE [Sketcher::SketchObject] Sketch002
  FullyConstrained = true
  sketch-geometry (20):
    g0: LineSegment StartX=-2.77179 StartY=-200.304 StartZ=0 EndX=5.22821 EndY=-200.304 EndZ=0
    g1: LineSegment StartX=5.22821 StartY=-200.304 StartZ=0 EndX=5.22821 EndY=-197.304 EndZ=0
    g2: LineSegment StartX=-2.77179 StartY=-200.304 StartZ=0 EndX=-2.77179 EndY=-197.304 EndZ=0
    g3: LineSegment StartX=5.22821 StartY=-197.304 StartZ=0 EndX=8.22821 EndY=-197.304 EndZ=0
    g4: LineSegment StartX=-2.77179 StartY=-197.304 StartZ=0 EndX=-5.77179 EndY=-197.304 EndZ=0
    g5: LineSegment StartX=19.2282 StartY=-203.304 StartZ=0 EndX=19.2282 EndY=-206.304 EndZ=0
    g6: LineSegment StartX=-16.7718 StartY=-203.304 StartZ=0 EndX=-16.7718 EndY=-206.304 EndZ=0
    g7: LineSegment StartX=-16.7718 StartY=-206.304 StartZ=0 EndX=19.2282 EndY=-206.304 EndZ=0
    g8: Circle CenterX=-16.7718 CenterY=-203.304 CenterZ=0 NormalX=0 NormalY=0 NormalZ=1 AngleXU=0 Radius=1
    g9: Circle CenterX=-5.77179 CenterY=-203.304 CenterZ=0 NormalX=0 NormalY=0 NormalZ=1 AngleXU=0 Radius=1
    g10: Circle CenterX=-5.77179 CenterY=-197.304 CenterZ=0 NormalX=0 NormalY=0 NormalZ=1 AngleXU=0 Radius=1
    g11: BSplineCurve PolesCount=3 KnotsCount=2 Degree=2 IsPeriodic=0
    g12: GeomPoint X=-16.7718 Y=-203.304 Z=0
    g13: GeomPoint X=-5.77179 Y=-197.304 Z=0
    g14: Circle CenterX=19.2282 CenterY=-203.304 CenterZ=0 NormalX=0 NormalY=0 NormalZ=1 AngleXU=0 Radius=1
    g15: Circle CenterX=8.22821 CenterY=-203.304 CenterZ=0 NormalX=0 NormalY=0 NormalZ=1 AngleXU=0 Radius=1
    g16: Circle CenterX=8.22821 CenterY=-197.304 CenterZ=0 NormalX=0 NormalY=0 NormalZ=1 AngleXU=0 Radius=1
    g17: BSplineCurve PolesCount=3 KnotsCount=2 Degree=2 IsPeriodic=0
    g18: GeomPoint X=19.2282 Y=-203.304 Z=0
    g19: GeomPoint X=8.22821 Y=-197.304 Z=0
  constraints (41):
    c: Horizontal(g0)
    c: Distance(g0) = 8
    c: Coincident(g1,g0)
    c: Vertical(g1)
    c: Distance(g1) = 3
    c: Coincident(g2,g0)
    c: Vertical(g2)
    c: Distance(g2) = 3
    c: Coincident(g3,g1)
    c: Horizontal(g3)
    c: Distance(g3) = 3
    c: Coincident(g4,g2)
    c: Horizontal(g4)
    c: Distance(g4) = 3
    c: Vertical(g5)
    c: Vertical(g6)
    c: Coincident(g7,g6)
    c: Coincident(g7,g5)
    c: Weight(g8) = 1
    c: Equal(g8,g9)
    c: Equal(g8,g10)
    c: Coincident(g11,g4)
    c: InternalAlignment(g8,g11)
    c: InternalAlignment(g9,g11)
    c: InternalAlignment(g10,g11)
    c: InternalAlignment(g12,g11)
    c: InternalAlignment(g13,g11)
    c: Coincident(g17,g5)
    c: Weight(g14) = 1
    c: Equal(g14,g15)
    c: Equal(g14,g16)
    c: Coincident(g17,g3)
    c: InternalAlignment(g14,g17)
    c: InternalAlignment(g15,g17)
    c: InternalAlignment(g16,g17)
    c: InternalAlignment(g18,g17)
    c: InternalAlignment(g19,g17)
    c: Block(g7)
    c: Block(g17)
    c: Block(g11)
    c: Block(g6)
FEATURE [Part::Extrusion] Extrude003
  Base = -> Sketch002
  Dir = (0,0,1)
  DirMode = 2
  FaceMakerClass = Part::FaceMakerBullseye
  LengthFwd = 260
  LengthRev = 0
  Solid = true
  Symmetric = false
FEATURE [Part::Extrusion] Extrude
  Base = -> Sketch
  Dir = (0,0,1)
  DirMode = 2
  FaceMakerClass = Part::FaceMakerBullseye
  LengthFwd = 14
  LengthRev = 0
  Solid = true
  Symmetric = false
FEATURE [Sketcher::SketchObject] Sketch003
  FullyConstrained = false
  sketch-geometry (351):
    g0: LineSegment StartX=-10.9272 StartY=-82.7794 StartZ=0 EndX=46.0728 EndY=-51.4823 EndZ=0
    g1: LineSegment StartX=-10.9272 StartY=76.4095 StartZ=0 EndX=-10.9272 EndY=-82.7794 EndZ=0
    g2: LineSegment StartX=46.0728 StartY=76.4095 StartZ=0 EndX=46.0728 EndY=-51.4823 EndZ=0
    g3: LineSegment StartX=-42.9272 StartY=136.221 StartZ=0 EndX=-42.9272 EndY=-103.779 EndZ=0
    g4: LineSegment StartX=407.073 StartY=136.221 StartZ=0 EndX=407.073 EndY=-103.779 EndZ=0
    g5: ArcOfCircle CenterX=-26.9272 CenterY=-83.7794 CenterZ=0 NormalX=0 NormalY=0 NormalZ=1 AngleXU=0 Radius=8 StartAngle=3.14159 EndAngle=6.28319
    g6: ArcOfCircle CenterX=391.073 CenterY=22.1087 CenterZ=0 NormalX=0 NormalY=0 NormalZ=1 AngleXU=0 Radius=8 StartAngle=7.05737e-08 EndAngle=3.14159
    g7: ArcOfCircle CenterX=391.073 CenterY=-83.7794 CenterZ=0 NormalX=0 NormalY=0 NormalZ=1 AngleXU=0 Radius=8 StartAngle=3.14159 EndAngle=6.28319
    g8: Circle CenterX=175.022 CenterY=27.0628 CenterZ=0 NormalX=0 NormalY=0 NormalZ=1 AngleXU=0 Radius=1
    g9: Circle CenterX=179.022 CenterY=24.8665 CenterZ=0 NormalX=0 NormalY=0 NormalZ=1 AngleXU=0 Radius=1
    g10: Circle CenterX=179.022 CenterY=27.0628 CenterZ=0 NormalX=0 NormalY=0 NormalZ=1 AngleXU=0 Radius=1
    g11: BSplineCurve PolesCount=3 KnotsCount=2 Degree=2 IsPeriodic=0
    g12: GeomPoint X=175.022 Y=27.0628 Z=0
    g13: GeomPoint X=179.022 Y=27.0628 Z=0
    g14: Circle CenterX=189.124 CenterY=27.0628 CenterZ=0 NormalX=0 NormalY=0 NormalZ=1 AngleXU=0 Radius=1
    g15: Circle CenterX=185.124 CenterY=24.8665 CenterZ=0 NormalX=0 NormalY=0 NormalZ=1 AngleXU=0 Radius=1
    g16: Circle CenterX=185.124 CenterY=27.0628 CenterZ=0 NormalX=0 NormalY=0 NormalZ=1 AngleXU=0 Radius=1
    g17: BSplineCurve PolesCount=3 KnotsCount=2 Degree=2 IsPeriodic=0
    g18: GeomPoint X=189.124 Y=27.0628 Z=0
    g19: GeomPoint X=185.124 Y=27.0628 Z=0
    g20: Circle CenterX=175.022 CenterY=5.37834 CenterZ=0 NormalX=0 NormalY=0 NormalZ=1 AngleXU=0 Radius=1
    g21: Circle CenterX=179.022 CenterY=7.57463 CenterZ=0 NormalX=0 NormalY=0 NormalZ=1 AngleXU=0 Radius=1
    g22: Circle CenterX=179.022 CenterY=5.34704 CenterZ=0 NormalX=0 NormalY=0 NormalZ=1 AngleXU=0 Radius=1
    g23: BSplineCurve PolesCount=3 KnotsCount=2 Degree=2 IsPeriodic=0
    g24: GeomPoint X=175.022 Y=5.37834 Z=0
    g25: GeomPoint X=179.022 Y=5.34704 Z=0
    g26: Circle CenterX=189.124 CenterY=5.37834 CenterZ=0 NormalX=0 NormalY=0 NormalZ=1 AngleXU=0 Radius=1
    g27: Circle CenterX=185.124 CenterY=7.57463 CenterZ=0 NormalX=0 NormalY=0 NormalZ=1 AngleXU=0 Radius=1
    g28: Circle CenterX=185.124 CenterY=5.34704 CenterZ=0 NormalX=0 NormalY=0 NormalZ=1 AngleXU=0 Radius=1
    g29: BSplineCurve PolesCount=3 KnotsCount=2 Degree=2 IsPeriodic=0
    g30: GeomPoint X=189.124 Y=5.37834 Z=0
    g31: GeomPoint X=185.124 Y=5.34704 Z=0
    g32: Circle CenterX=165.871 CenterY=18.1458 CenterZ=0 NormalX=0 NormalY=0 NormalZ=1 AngleXU=0 Radius=1
    g33: Circle CenterX=169.377 CenterY=16.2206 CenterZ=0 NormalX=0 NormalY=0 NormalZ=1 AngleXU=0 Radius=1
    g34: Circle CenterX=165.871 CenterY=14.2954 CenterZ=0 NormalX=0 NormalY=0 NormalZ=1 AngleXU=0 Radius=1
    g35: BSplineCurve PolesCount=3 KnotsCount=2 Degree=2 IsPeriodic=0
    g36: GeomPoint X=165.871 Y=18.1458 Z=0
    g37: GeomPoint X=165.871 Y=14.2954 Z=0
    g38: Circle CenterX=198.275 CenterY=18.1458 CenterZ=0 NormalX=0 NormalY=0 NormalZ=1 AngleXU=0 Radius=1
    g39: Circle CenterX=194.768 CenterY=16.2206 CenterZ=0 NormalX=0 NormalY=0 NormalZ=1 AngleXU=0 Radius=1
    g40: Circle CenterX=198.275 CenterY=14.2954 CenterZ=0 NormalX=0 NormalY=0 NormalZ=1 AngleXU=0 Radius=1
    g41: BSplineCurve PolesCount=3 KnotsCount=2 Degree=2 IsPeriodic=0
    g42: GeomPoint X=198.275 Y=18.1458 Z=0
    g43: GeomPoint X=198.275 Y=14.2954 Z=0
    g44: LineSegment StartX=407.073 StartY=-103.779 StartZ=0 EndX=-42.9272 EndY=-103.779 EndZ=0
    g45: LineSegment StartX=407.073 StartY=136.221 StartZ=0 EndX=-42.9272 EndY=136.221 EndZ=0
    g46: LineSegment StartX=46.0728 StartY=76.4095 StartZ=0 EndX=-10.9272 EndY=76.4095 EndZ=0
    g47: Circle CenterX=125.607 CenterY=54.1951 CenterZ=0 NormalX=0 NormalY=0 NormalZ=1 AngleXU=0 Radius=1
    g48: Circle CenterX=139.632 CenterY=46.4944 CenterZ=0 NormalX=0 NormalY=0 NormalZ=1 AngleXU=0 Radius=1
    g49: Circle CenterX=127.326 CenterY=56.7187 CenterZ=0 NormalX=0 NormalY=0 NormalZ=1 AngleXU=0 Radius=1
    g50: BSplineCurve PolesCount=3 KnotsCount=2 Degree=2 IsPeriodic=0
    g51: GeomPoint X=125.607 Y=54.1951 Z=0
    g52: GeomPoint X=127.326 Y=56.7187 Z=0
    g53: Circle CenterX=236.821 CenterY=56.7187 CenterZ=0 NormalX=0 NormalY=0 NormalZ=1 AngleXU=0 Radius=1
    g54: Circle CenterX=224.513 CenterY=46.4944 CenterZ=0 NormalX=0 NormalY=0 NormalZ=1 AngleXU=0 Radius=1
    g55: Circle CenterX=238.538 CenterY=54.1951 CenterZ=0 NormalX=0 NormalY=0 NormalZ=1 AngleXU=0 Radius=1
    g56: BSplineCurve PolesCount=3 KnotsCount=2 Degree=2 IsPeriodic=0
    g57: GeomPoint X=236.821 Y=56.7187 Z=0
    g58: GeomPoint X=238.538 Y=54.1951 Z=0
    g59: Circle CenterX=238.538 CenterY=-21.7539 CenterZ=0 NormalX=0 NormalY=0 NormalZ=1 AngleXU=0 Radius=1
    g60: Circle CenterX=224.513 CenterY=-14.0532 CenterZ=0 NormalX=0 NormalY=0 NormalZ=1 AngleXU=0 Radius=1
    g61: Circle CenterX=236.821 CenterY=-24.2775 CenterZ=0 NormalX=0 NormalY=0 NormalZ=1 AngleXU=0 Radius=1
    g62: BSplineCurve PolesCount=3 KnotsCount=2 Degree=2 IsPeriodic=0
    g63: GeomPoint X=238.538 Y=-21.7539 Z=0
    g64: GeomPoint X=236.821 Y=-24.2775 Z=0
    g65: Circle CenterX=125.607 CenterY=-21.7539 CenterZ=0 NormalX=0 NormalY=0 NormalZ=1 AngleXU=0 Radius=1
    g66: Circle CenterX=139.632 CenterY=-14.0532 CenterZ=0 NormalX=0 NormalY=0 NormalZ=1 AngleXU=0 Radius=1
    g67: Circle CenterX=127.325 CenterY=-24.2775 CenterZ=0 NormalX=0 NormalY=0 NormalZ=1 AngleXU=0 Radius=1
    g68: BSplineCurve PolesCount=3 KnotsCount=2 Degree=2 IsPeriodic=0
    g69: GeomPoint X=125.607 Y=-21.7539 Z=0
    g70: GeomPoint X=127.325 Y=-24.2775 Z=0
    g71: Circle CenterX=302.996 CenterY=111.695 CenterZ=0 NormalX=0 NormalY=0 NormalZ=1 AngleXU=0 Radius=1
    g72: Circle CenterX=306.073 CenterY=114.251 CenterZ=0 NormalX=0 NormalY=0 NormalZ=1 AngleXU=0 Radius=1
    g73: Circle CenterX=306.073 CenterY=110.251 CenterZ=0 NormalX=0 NormalY=0 NormalZ=1 AngleXU=0 Radius=1
    g74: BSplineCurve PolesCount=3 KnotsCount=2 Degree=2 IsPeriodic=0
    g75: GeomPoint X=302.996 Y=111.695 Z=0
    g76: GeomPoint X=306.073 Y=110.251 Z=0
    g77: Circle CenterX=306.073 CenterY=95.2763 CenterZ=0 NormalX=0 NormalY=0 NormalZ=1 AngleXU=0 Radius=1
    g78: Circle CenterX=306.073 CenterY=91.2763 CenterZ=0 NormalX=0 NormalY=0 NormalZ=1 AngleXU=0 Radius=1
    g79: Circle CenterX=302.567 CenterY=89.3511 CenterZ=0 NormalX=0 NormalY=0 NormalZ=1 AngleXU=0 Radius=1
    g80: BSplineCurve PolesCount=3 KnotsCount=2 Degree=2 IsPeriodic=0
    g81: GeomPoint X=306.073 Y=95.2763 Z=0
    g82: GeomPoint X=302.567 Y=89.3511 Z=0
    g83: LineSegment StartX=306.073 StartY=110.251 StartZ=0 EndX=306.073 EndY=95.2763 EndZ=0
    g84: LineSegment StartX=302.996 StartY=111.695 StartZ=0 EndX=236.821 EndY=56.7187 EndZ=0
    g85: LineSegment StartX=238.538 StartY=54.1951 StartZ=0 EndX=302.567 EndY=89.3511 EndZ=0
    g86: Circle CenterX=61.1496 CenterY=111.695 CenterZ=0 NormalX=0 NormalY=0 NormalZ=1 AngleXU=0 Radius=1
    g87: Circle CenterX=58.0728 CenterY=114.251 CenterZ=0 NormalX=0 NormalY=0 NormalZ=1 AngleXU=0 Radius=1
    g88: Circle CenterX=58.0728 CenterY=110.251 CenterZ=0 NormalX=0 NormalY=0 NormalZ=1 AngleXU=0 Radius=1
    g89: BSplineCurve PolesCount=3 KnotsCount=2 Degree=2 IsPeriodic=0
    g90: GeomPoint X=61.1496 Y=111.695 Z=0
    g91: GeomPoint X=58.0728 Y=110.251 Z=0
    g92: Circle CenterX=61.5791 CenterY=89.3511 CenterZ=0 NormalX=0 NormalY=0 NormalZ=1 AngleXU=0 Radius=1
    g93: Circle CenterX=58.0728 CenterY=91.2763 CenterZ=0 NormalX=0 NormalY=0 NormalZ=1 AngleXU=0 Radius=1
    g94: Circle CenterX=58.0728 CenterY=95.2763 CenterZ=0 NormalX=0 NormalY=0 NormalZ=1 AngleXU=0 Radius=1
    g95: BSplineCurve PolesCount=3 KnotsCount=2 Degree=2 IsPeriodic=0
    g96: GeomPoint X=61.5791 Y=89.3511 Z=0
    g97: GeomPoint X=58.0728 Y=95.2763 Z=0
    g98: LineSegment StartX=58.0728 StartY=110.251 StartZ=0 EndX=58.0728 EndY=95.2763 EndZ=0
    g99: LineSegment StartX=61.1496 StartY=111.695 StartZ=0 EndX=127.326 EndY=56.7187 EndZ=0
    g100: LineSegment StartX=125.607 StartY=54.1951 StartZ=0 EndX=61.5791 EndY=89.3511 EndZ=0
    g101: Circle CenterX=61.5791 CenterY=-56.9099 CenterZ=0 NormalX=0 NormalY=0 NormalZ=1 AngleXU=0 Radius=1
    g102: Circle CenterX=58.0728 CenterY=-58.8351 CenterZ=0 NormalX=0 NormalY=0 NormalZ=1 AngleXU=0 Radius=1
    g103: Circle CenterX=58.0728 CenterY=-62.8351 CenterZ=0 NormalX=0 NormalY=0 NormalZ=1 AngleXU=0 Radius=1
    g104: BSplineCurve PolesCount=3 KnotsCount=2 Degree=2 IsPeriodic=0
    g105: GeomPoint X=61.5791 Y=-56.9099 Z=0
    g106: GeomPoint X=58.0728 Y=-62.8351 Z=0
    g107: Circle CenterX=58.0728 CenterY=-77.8102 CenterZ=0 NormalX=0 NormalY=0 NormalZ=1 AngleXU=0 Radius=1
    g108: Circle CenterX=58.0728 CenterY=-81.8102 CenterZ=0 NormalX=0 NormalY=0 NormalZ=1 AngleXU=0 Radius=1
    g109: Circle CenterX=61.1496 CenterY=-79.2541 CenterZ=0 NormalX=0 NormalY=0 NormalZ=1 AngleXU=0 Radius=1
    g110: BSplineCurve PolesCount=3 KnotsCount=2 Degree=2 IsPeriodic=0
    g111: GeomPoint X=58.0728 Y=-77.8102 Z=0
    g112: GeomPoint X=61.1496 Y=-79.2541 Z=0
    g113: LineSegment StartX=58.0728 StartY=-62.8351 StartZ=0 EndX=58.0728 EndY=-77.8102 EndZ=0
    g114: LineSegment StartX=61.1496 StartY=-79.2541 StartZ=0 EndX=127.325 EndY=-24.2775 EndZ=0
    g115: LineSegment StartX=125.607 StartY=-21.7539 StartZ=0 EndX=61.5791 EndY=-56.9099 EndZ=0
    g116: Circle CenterX=302.567 CenterY=-56.9099 CenterZ=0 NormalX=0 NormalY=0 NormalZ=1 AngleXU=0 Radius=1
    g117: Circle CenterX=306.073 CenterY=-58.8351 CenterZ=0 NormalX=0 NormalY=0 NormalZ=1 AngleXU=0 Radius=1
    g118: Circle CenterX=306.073 CenterY=-62.8351 CenterZ=0 NormalX=0 NormalY=0 NormalZ=1 AngleXU=0 Radius=1
    g119: BSplineCurve PolesCount=3 KnotsCount=2 Degree=2 IsPeriodic=0
    g120: GeomPoint X=302.567 Y=-56.9099 Z=0
    g121: GeomPoint X=306.073 Y=-62.8351 Z=0
    g122: Circle CenterX=302.996 CenterY=-79.2541 CenterZ=0 NormalX=0 NormalY=0 NormalZ=1 AngleXU=0 Radius=1
    g123: Circle CenterX=306.073 CenterY=-81.8102 CenterZ=0 NormalX=0 NormalY=0 NormalZ=1 AngleXU=0 Radius=1
    g124: Circle CenterX=306.073 CenterY=-77.8102 CenterZ=0 NormalX=0 NormalY=0 NormalZ=1 AngleXU=0 Radius=1
    g125: BSplineCurve PolesCount=3 KnotsCount=2 Degree=2 IsPeriodic=0
    g126: GeomPoint X=302.996 Y=-79.2541 Z=0
    g127: GeomPoint X=306.073 Y=-77.8102 Z=0
    g128: LineSegment StartX=306.073 StartY=-62.8351 StartZ=0 EndX=306.073 EndY=-77.8102 EndZ=0
    g129: LineSegment StartX=302.996 StartY=-79.2541 StartZ=0 EndX=236.821 EndY=-24.2775 EndZ=0
    g130: LineSegment StartX=238.538 StartY=-21.7539 StartZ=0 EndX=302.567 EndY=-56.9099 EndZ=0
    g131: Circle CenterX=61.6457 CenterY=-88.8112 CenterZ=0 NormalX=0 NormalY=0 NormalZ=1 AngleXU=0 Radius=1
    g132: Circle CenterX=58.0728 CenterY=-91.7794 CenterZ=0 NormalX=0 NormalY=0 NormalZ=1 AngleXU=0 Radius=1
    g133: Circle CenterX=63.9135 CenterY=-91.7794 CenterZ=0 NormalX=0 NormalY=0 NormalZ=1 AngleXU=0 Radius=1
    g134: BSplineCurve PolesCount=3 KnotsCount=2 Degree=2 IsPeriodic=0
    g135: GeomPoint X=61.6457 Y=-88.8112 Z=0
    g136: GeomPoint X=63.9135 Y=-91.7794 Z=0
    g137: Circle CenterX=179.022 CenterY=-85.8163 CenterZ=0 NormalX=0 NormalY=0 NormalZ=1 AngleXU=0 Radius=1
    g138: Circle CenterX=179.022 CenterY=-91.7794 CenterZ=0 NormalX=0 NormalY=0 NormalZ=1 AngleXU=0 Radius=1
    g139: Circle CenterX=171.895 CenterY=-91.7794 CenterZ=0 NormalX=0 NormalY=0 NormalZ=1 AngleXU=0 Radius=1
    g140: BSplineCurve PolesCount=3 KnotsCount=2 Degree=2 IsPeriodic=0
    g141: GeomPoint X=179.022 Y=-85.8163 Z=0
    g142: GeomPoint X=171.895 Y=-91.7794 Z=0
    g143: Circle CenterX=185.124 CenterY=-86.2028 CenterZ=0 NormalX=0 NormalY=0 NormalZ=1 AngleXU=0 Radius=1
    g144: Circle CenterX=185.124 CenterY=-91.7794 CenterZ=0 NormalX=0 NormalY=0 NormalZ=1 AngleXU=0 Radius=1
    g145: Circle CenterX=191.747 CenterY=-91.7794 CenterZ=0 NormalX=0 NormalY=0 NormalZ=1 AngleXU=0 Radius=1
    g146: BSplineCurve PolesCount=3 KnotsCount=2 Degree=2 IsPeriodic=0
    g147: GeomPoint X=185.124 Y=-86.2028 Z=0
    g148: GeomPoint X=191.747 Y=-91.7794 Z=0
    g149: Circle CenterX=299.888 CenterY=-86.6413 CenterZ=0 NormalX=0 NormalY=0 NormalZ=1 AngleXU=0 Radius=1
    g150: Circle CenterX=306.073 CenterY=-91.7794 CenterZ=0 NormalX=0 NormalY=0 NormalZ=1 AngleXU=0 Radius=1
    g151: Circle CenterX=298.776 CenterY=-91.7794 CenterZ=0 NormalX=0 NormalY=0 NormalZ=1 AngleXU=0 Radius=1
    g152: BSplineCurve PolesCount=3 KnotsCount=2 Degree=2 IsPeriodic=0
    g153: GeomPoint X=299.888 Y=-86.6413 Z=0
    g154: GeomPoint X=298.776 Y=-91.7794 Z=0
    g155: LineSegment StartX=189.124 StartY=5.37834 StartZ=0 EndX=299.888 EndY=-86.6413 EndZ=0
    g156: LineSegment StartX=298.776 StartY=-91.7794 StartZ=0 EndX=191.747 EndY=-91.7794 EndZ=0
    g157: LineSegment StartX=185.124 StartY=-86.2028 StartZ=0 EndX=185.124 EndY=5.34704 EndZ=0
    g158: LineSegment StartX=179.022 StartY=5.34704 StartZ=0 EndX=179.022 EndY=-85.8163 EndZ=0
    g159: LineSegment StartX=171.895 StartY=-91.7794 StartZ=0 EndX=63.9135 EndY=-91.7794 EndZ=0
    g160: LineSegment StartX=61.6457 StartY=-88.8112 StartZ=0 EndX=175.022 EndY=5.37834 EndZ=0
    g161: Circle CenterX=302.073 CenterY=124.221 CenterZ=0 NormalX=0 NormalY=0 NormalZ=1 AngleXU=0 Radius=1
    g162: Circle CenterX=306.073 CenterY=124.221 CenterZ=0 NormalX=0 NormalY=0 NormalZ=1 AngleXU=0 Radius=1
    g163: Circle CenterX=302.996 CenterY=121.665 CenterZ=0 NormalX=0 NormalY=0 NormalZ=1 AngleXU=0 Radius=1
    g164: BSplineCurve PolesCount=3 KnotsCount=2 Degree=2 IsPeriodic=0
    g165: GeomPoint X=302.073 Y=124.221 Z=0
    g166: GeomPoint X=302.996 Y=121.665 Z=0
    g167: Circle CenterX=189.124 CenterY=124.221 CenterZ=0 NormalX=0 NormalY=0 NormalZ=1 AngleXU=0 Radius=1
    g168: Circle CenterX=185.124 CenterY=124.221 CenterZ=0 NormalX=0 NormalY=0 NormalZ=1 AngleXU=0 Radius=1
    g169: Circle CenterX=185.124 CenterY=120.221 CenterZ=0 NormalX=0 NormalY=0 NormalZ=1 AngleXU=0 Radius=1
    g170: BSplineCurve PolesCount=3 KnotsCount=2 Degree=2 IsPeriodic=0
    g171: GeomPoint X=189.124 Y=124.221 Z=0
    g172: GeomPoint X=185.124 Y=120.221 Z=0
    g173: Circle CenterX=175.022 CenterY=124.221 CenterZ=0 NormalX=0 NormalY=0 NormalZ=1 AngleXU=0 Radius=1
    g174: Circle CenterX=179.022 CenterY=124.221 CenterZ=0 NormalX=0 NormalY=0 NormalZ=1 AngleXU=0 Radius=1
    g175: Circle CenterX=179.022 CenterY=120.221 CenterZ=0 NormalX=0 NormalY=0 NormalZ=1 AngleXU=0 Radius=1
    g176: BSplineCurve PolesCount=3 KnotsCount=2 Degree=2 IsPeriodic=0
    g177: GeomPoint X=175.022 Y=124.221 Z=0
    g178: GeomPoint X=179.022 Y=120.221 Z=0
    g179: Circle CenterX=62.0728 CenterY=124.221 CenterZ=0 NormalX=0 NormalY=0 NormalZ=1 AngleXU=0 Radius=1
    g180: Circle CenterX=58.0728 CenterY=124.221 CenterZ=0 NormalX=0 NormalY=0 NormalZ=1 AngleXU=0 Radius=1
    g181: Circle CenterX=61.1496 CenterY=121.665 CenterZ=0 NormalX=0 NormalY=0 NormalZ=1 AngleXU=0 Radius=1
    g182: BSplineCurve PolesCount=3 KnotsCount=2 Degree=2 IsPeriodic=0
    g183: GeomPoint X=62.0728 Y=124.221 Z=0
    g184: GeomPoint X=61.1496 Y=121.665 Z=0
    g185: LineSegment StartX=62.0728 StartY=124.221 StartZ=0 EndX=175.022 EndY=124.221 EndZ=0
    g186: LineSegment StartX=179.022 StartY=120.221 StartZ=0 EndX=179.022 EndY=27.0628 EndZ=0
    g187: LineSegment StartX=185.124 StartY=27.0628 StartZ=0 EndX=185.124 EndY=120.221 EndZ=0
    g188: LineSegment StartX=189.124 StartY=124.221 StartZ=0 EndX=302.073 EndY=124.221 EndZ=0
    g189: LineSegment StartX=302.996 StartY=121.665 StartZ=0 EndX=189.124 EndY=27.0628 EndZ=0
    g190: LineSegment StartX=175.022 StartY=27.0628 StartZ=0 EndX=61.1496 EndY=121.665 EndZ=0
    g191: Circle CenterX=61.5791 CenterY=75.4095 CenterZ=0 NormalX=0 NormalY=0 NormalZ=1 AngleXU=0 Radius=1
    g192: Circle CenterX=58.0728 CenterY=77.3346 CenterZ=0 NormalX=0 NormalY=0 NormalZ=1 AngleXU=0 Radius=1
    g193: Circle CenterX=58.0728 CenterY=73.3346 CenterZ=0 NormalX=0 NormalY=0 NormalZ=1 AngleXU=0 Radius=1
    g194: BSplineCurve PolesCount=3 KnotsCount=2 Degree=2 IsPeriodic=0
    g195: GeomPoint X=61.5791 Y=75.4095 Z=0
    g196: GeomPoint X=58.0728 Y=73.3346 Z=0
    g197: Circle CenterX=58.0728 CenterY=-40.8935 CenterZ=0 NormalX=0 NormalY=0 NormalZ=1 AngleXU=0 Radius=1
    g198: Circle CenterX=58.0728 CenterY=-44.8935 CenterZ=0 NormalX=0 NormalY=0 NormalZ=1 AngleXU=0 Radius=1
    g199: Circle CenterX=61.5791 CenterY=-42.9683 CenterZ=0 NormalX=0 NormalY=0 NormalZ=1 AngleXU=0 Radius=1
    g200: BSplineCurve PolesCount=3 KnotsCount=2 Degree=2 IsPeriodic=0
    g201: GeomPoint X=58.0728 Y=-40.8935 Z=0
    g202: GeomPoint X=61.5791 Y=-42.9683 Z=0
    g203: LineSegment StartX=61.5791 StartY=-42.9683 StartZ=0 EndX=165.871 EndY=14.2954 EndZ=0
    g204: LineSegment StartX=165.871 StartY=18.1458 StartZ=0 EndX=61.5791 EndY=75.4095 EndZ=0
    g205: LineSegment StartX=58.0728 StartY=73.3346 StartZ=0 EndX=58.0728 EndY=-40.8935 EndZ=0
    g206: Circle CenterX=302.567 CenterY=-42.9683 CenterZ=0 NormalX=0 NormalY=0 NormalZ=1 AngleXU=0 Radius=1
    g207: Circle CenterX=306.073 CenterY=-44.8935 CenterZ=0 NormalX=0 NormalY=0 NormalZ=1 AngleXU=0 Radius=1
    g208: Circle CenterX=306.073 CenterY=-40.8935 CenterZ=0 NormalX=0 NormalY=0 NormalZ=1 AngleXU=0 Radius=1
    g209: BSplineCurve PolesCount=3 KnotsCount=2 Degree=2 IsPeriodic=0
    g210: GeomPoint X=302.567 Y=-42.9683 Z=0
    g211: GeomPoint X=306.073 Y=-40.8935 Z=0
    g212: Circle CenterX=306.073 CenterY=73.3346 CenterZ=0 NormalX=0 NormalY=0 NormalZ=1 AngleXU=0 Radius=1
    g213: Circle CenterX=306.073 CenterY=77.3346 CenterZ=0 NormalX=0 NormalY=0 NormalZ=1 AngleXU=0 Radius=1
    g214: Circle CenterX=302.567 CenterY=75.4095 CenterZ=0 NormalX=0 NormalY=0 NormalZ=1 AngleXU=0 Radius=1
    g215: BSplineCurve PolesCount=3 KnotsCount=2 Degree=2 IsPeriodic=0
    g216: GeomPoint X=306.073 Y=73.3346 Z=0
    g217: GeomPoint X=302.567 Y=75.4095 Z=0
    g218: LineSegment StartX=302.567 StartY=-42.9683 StartZ=0 EndX=198.275 EndY=14.2954 EndZ=0
    g219: LineSegment StartX=198.275 StartY=18.1458 StartZ=0 EndX=302.567 EndY=75.4095 EndZ=0
    g220: LineSegment StartX=306.073 StartY=73.3346 StartZ=0 EndX=306.073 EndY=-40.8935 EndZ=0
    g221: LineSegment StartX=322.073 StartY=105.865 StartZ=0 EndX=328.643 EndY=105.865 EndZ=0
    g222: LineSegment StartX=318.073 StartY=120.221 StartZ=0 EndX=318.073 EndY=109.865 EndZ=0
    g223: LineSegment StartX=336.157 StartY=107.779 StartZ=0 EndX=362.567 EndY=122.294 EndZ=0
    g224: Circle CenterX=362.073 CenterY=124.221 CenterZ=0 NormalX=0 NormalY=0 NormalZ=1 AngleXU=0 Radius=1
    g225: Circle CenterX=366.073 CenterY=124.221 CenterZ=0 NormalX=0 NormalY=0 NormalZ=1 AngleXU=0 Radius=1
    g226: Circle CenterX=362.567 CenterY=122.294 CenterZ=0 NormalX=0 NormalY=0 NormalZ=1 AngleXU=0 Radius=1
    g227: BSplineCurve PolesCount=3 KnotsCount=2 Degree=2 IsPeriodic=0
    g228: GeomPoint X=362.073 Y=124.221 Z=0
    g229: GeomPoint X=362.567 Y=122.294 Z=0
    g230: Circle CenterX=322.073 CenterY=124.221 CenterZ=0 NormalX=0 NormalY=0 NormalZ=1 AngleXU=0 Radius=1
    g231: Circle CenterX=318.073 CenterY=124.221 CenterZ=0 NormalX=0 NormalY=0 NormalZ=1 AngleXU=0 Radius=1
    g232: Circle CenterX=318.073 CenterY=120.221 CenterZ=0 NormalX=0 NormalY=0 NormalZ=1 AngleXU=0 Radius=1
    g233: BSplineCurve PolesCount=3 KnotsCount=2 Degree=2 IsPeriodic=0
    g234: GeomPoint X=322.073 Y=124.221 Z=0
    g235: GeomPoint X=318.073 Y=120.221 Z=0
    g236: Circle CenterX=322.073 CenterY=105.865 CenterZ=0 NormalX=0 NormalY=0 NormalZ=1 AngleXU=0 Radius=1
    g237: Circle CenterX=318.073 CenterY=105.865 CenterZ=0 NormalX=0 NormalY=0 NormalZ=1 AngleXU=0 Radius=1
    g238: Circle CenterX=318.073 CenterY=109.865 CenterZ=0 NormalX=0 NormalY=0 NormalZ=1 AngleXU=0 Radius=1
    g239: BSplineCurve PolesCount=3 KnotsCount=2 Degree=2 IsPeriodic=0
    g240: GeomPoint X=322.073 Y=105.865 Z=0
    g241: GeomPoint X=318.073 Y=109.865 Z=0
    g242: Circle CenterX=336.157 CenterY=107.779 CenterZ=0 NormalX=0 NormalY=0 NormalZ=1 AngleXU=0 Radius=1
    g243: Circle CenterX=332.651 CenterY=105.853 CenterZ=0 NormalX=0 NormalY=0 NormalZ=1 AngleXU=0 Radius=1
    g244: Circle CenterX=328.643 CenterY=105.865 CenterZ=0 NormalX=0 NormalY=0 NormalZ=1 AngleXU=0 Radius=1
    g245: BSplineCurve PolesCount=3 KnotsCount=2 Degree=2 IsPeriodic=0
    g246: GeomPoint X=336.157 Y=107.779 Z=0
    g247: GeomPoint X=328.643 Y=105.865 Z=0
    g248: LineSegment StartX=322.073 StartY=124.221 StartZ=0 EndX=362.073 EndY=124.221 EndZ=0
    g249: Circle CenterX=371.567 CenterY=-80.8644 CenterZ=0 NormalX=0 NormalY=0 NormalZ=1 AngleXU=0 Radius=1
    g250: Circle CenterX=375.073 CenterY=-82.7896 CenterZ=0 NormalX=0 NormalY=0 NormalZ=1 AngleXU=0 Radius=1
    g251: Circle CenterX=375.073 CenterY=-78.7896 CenterZ=0 NormalX=0 NormalY=0 NormalZ=1 AngleXU=0 Radius=1
    g252: BSplineCurve PolesCount=3 KnotsCount=2 Degree=2 IsPeriodic=0
    g253: GeomPoint X=371.567 Y=-80.8644 Z=0
    g254: GeomPoint X=375.073 Y=-78.7896 Z=0
    g255: Circle CenterX=321.579 CenterY=-53.4075 CenterZ=0 NormalX=0 NormalY=0 NormalZ=1 AngleXU=0 Radius=1
    g256: Circle CenterX=318.073 CenterY=-51.4823 CenterZ=0 NormalX=0 NormalY=0 NormalZ=1 AngleXU=0 Radius=1
    g257: Circle CenterX=318.073 CenterY=-47.4805 CenterZ=0 NormalX=0 NormalY=0 NormalZ=1 AngleXU=0 Radius=1
    g258: BSplineCurve PolesCount=3 KnotsCount=2 Degree=2 IsPeriodic=0
    g259: GeomPoint X=321.579 Y=-53.4075 Z=0
    g260: GeomPoint X=318.073 Y=-47.4805 Z=0
    g261: LineSegment StartX=371.567 StartY=-80.8644 StartZ=0 EndX=321.579 EndY=-53.4075 EndZ=0
    g262: Circle CenterX=321.579 CenterY=-67.3492 CenterZ=0 NormalX=0 NormalY=0 NormalZ=1 AngleXU=0 Radius=1
    g263: Circle CenterX=318.073 CenterY=-65.424 CenterZ=0 NormalX=0 NormalY=0 NormalZ=1 AngleXU=0 Radius=1
    g264: Circle CenterX=318.073 CenterY=-69.424 CenterZ=0 NormalX=0 NormalY=0 NormalZ=1 AngleXU=0 Radius=1
    g265: BSplineCurve PolesCount=3 KnotsCount=2 Degree=2 IsPeriodic=0
    g266: GeomPoint X=321.579 Y=-67.3492 Z=0
    g267: GeomPoint X=318.073 Y=-69.424 Z=0
    g268: Circle CenterX=362.567 CenterY=-89.8542 CenterZ=0 NormalX=0 NormalY=0 NormalZ=1 AngleXU=0 Radius=1
    g269: Circle CenterX=366.073 CenterY=-91.7794 CenterZ=0 NormalX=0 NormalY=0 NormalZ=1 AngleXU=0 Radius=1
    g270: Circle CenterX=362.073 CenterY=-91.7794 CenterZ=0 NormalX=0 NormalY=0 NormalZ=1 AngleXU=0 Radius=1
    g271: BSplineCurve PolesCount=3 KnotsCount=2 Degree=2 IsPeriodic=0
    g272: GeomPoint X=362.567 Y=-89.8542 Z=0
    g273: GeomPoint X=362.073 Y=-91.7794 Z=0
    g274: Circle CenterX=322.073 CenterY=-91.7794 CenterZ=0 NormalX=0 NormalY=0 NormalZ=1 AngleXU=0 Radius=1
    g275: Circle CenterX=318.073 CenterY=-91.7794 CenterZ=0 NormalX=0 NormalY=0 NormalZ=1 AngleXU=0 Radius=1
    g276: Circle CenterX=318.073 CenterY=-87.7794 CenterZ=0 NormalX=0 NormalY=0 NormalZ=1 AngleXU=0 Radius=1
    g277: BSplineCurve PolesCount=3 KnotsCount=2 Degree=2 IsPeriodic=0
    g278: GeomPoint X=322.073 Y=-91.7794 Z=0
    g279: GeomPoint X=318.073 Y=-87.7794 Z=0
    g280: LineSegment StartX=362.567 StartY=-89.8542 StartZ=0 EndX=321.579 EndY=-67.3492 EndZ=0
    g281: LineSegment StartX=318.073 StartY=-69.424 StartZ=0 EndX=318.073 EndY=-87.7794 EndZ=0
    g282: LineSegment StartX=322.073 StartY=-91.7794 StartZ=0 EndX=362.073 EndY=-91.7794 EndZ=0
    g283: Circle CenterX=2.07281 CenterY=124.221 CenterZ=0 NormalX=0 NormalY=0 NormalZ=1 AngleXU=0 Radius=1
    g284: Circle CenterX=1.57905 CenterY=122.295 CenterZ=0 NormalX=0 NormalY=0 NormalZ=1 AngleXU=0 Radius=1
    g285: BSplineCurve PolesCount=3 KnotsCount=2 Degree=2 IsPeriodic=0
    g286: GeomPoint X=2.07281 Y=124.221 Z=0
    g287: GeomPoint X=1.57905 Y=122.295 Z=0
    g288: Circle CenterX=42.0728 CenterY=124.221 CenterZ=0 NormalX=0 NormalY=0 NormalZ=1 AngleXU=0 Radius=1
    g289: Circle CenterX=46.0728 CenterY=124.221 CenterZ=0 NormalX=0 NormalY=0 NormalZ=1 AngleXU=0 Radius=1
    g290: Circle CenterX=46.0728 CenterY=120.221 CenterZ=0 NormalX=0 NormalY=0 NormalZ=1 AngleXU=0 Radius=1
    g291: BSplineCurve PolesCount=3 KnotsCount=2 Degree=2 IsPeriodic=0
    g292: GeomPoint X=42.0728 Y=124.221 Z=0
    g293: GeomPoint X=46.0728 Y=120.221 Z=0
    g294: Circle CenterX=46.0728 CenterY=109.865 CenterZ=0 NormalX=0 NormalY=0 NormalZ=1 AngleXU=0 Radius=1
    g295: Circle CenterX=46.0728 CenterY=105.865 CenterZ=0 NormalX=0 NormalY=0 NormalZ=1 AngleXU=0 Radius=1
    g296: Circle CenterX=42.0728 CenterY=105.865 CenterZ=0 NormalX=0 NormalY=0 NormalZ=1 AngleXU=0 Radius=1
    g297: BSplineCurve PolesCount=3 KnotsCount=2 Degree=2 IsPeriodic=0
    g298: GeomPoint X=46.0728 Y=109.865 Z=0
    g299: GeomPoint X=42.0728 Y=105.865 Z=0
    g300: Circle CenterX=35.5028 CenterY=105.865 CenterZ=0 NormalX=0 NormalY=0 NormalZ=1 AngleXU=0 Radius=1
    g301: Circle CenterX=31.5028 CenterY=105.865 CenterZ=0 NormalX=0 NormalY=0 NormalZ=1 AngleXU=0 Radius=1
    g302: Circle CenterX=27.9965 CenterY=107.79 CenterZ=0 NormalX=0 NormalY=0 NormalZ=1 AngleXU=0 Radius=1
    g303: BSplineCurve PolesCount=3 KnotsCount=2 Degree=2 IsPeriodic=0
    g304: GeomPoint X=35.5028 Y=105.865 Z=0
    g305: GeomPoint X=27.9965 Y=107.79 Z=0
    g306: LineSegment StartX=2.07281 StartY=124.221 StartZ=0 EndX=42.0728 EndY=124.221 EndZ=0
    g307: LineSegment StartX=46.0728 StartY=120.221 StartZ=0 EndX=46.0728 EndY=109.865 EndZ=0
    g308: LineSegment StartX=42.0728 StartY=105.865 StartZ=0 EndX=35.5028 EndY=105.865 EndZ=0
    g309: LineSegment StartX=27.9965 StartY=107.79 StartZ=0 EndX=1.57905 EndY=122.295 EndZ=0
    g310: Circle CenterX=42.5666 CenterY=-67.3492 CenterZ=0 NormalX=0 NormalY=0 NormalZ=1 AngleXU=0 Radius=1
    g311: Circle CenterX=46.0728 CenterY=-65.424 CenterZ=0 NormalX=0 NormalY=0 NormalZ=1 AngleXU=0 Radius=1
    g312: Circle CenterX=46.0728 CenterY=-69.424 CenterZ=0 NormalX=0 NormalY=0 NormalZ=1 AngleXU=0 Radius=1
    g313: BSplineCurve PolesCount=3 KnotsCount=2 Degree=2 IsPeriodic=0
    g314: GeomPoint X=42.5666 Y=-67.3492 Z=0
    g315: GeomPoint X=46.0728 Y=-69.424 Z=0
    g316: Circle CenterX=46.0728 CenterY=-87.7794 CenterZ=0 NormalX=0 NormalY=0 NormalZ=1 AngleXU=0 Radius=1
    g317: Circle CenterX=46.0728 CenterY=-91.7794 CenterZ=0 NormalX=0 NormalY=0 NormalZ=1 AngleXU=0 Radius=1
    g318: Circle CenterX=42.0728 CenterY=-91.7794 CenterZ=0 NormalX=0 NormalY=0 NormalZ=1 AngleXU=0 Radius=1
    g319: BSplineCurve PolesCount=3 KnotsCount=2 Degree=2 IsPeriodic=0
    g320: GeomPoint X=46.0728 Y=-87.7794 Z=0
    g321: GeomPoint X=42.0728 Y=-91.7794 Z=0
    g322: Circle CenterX=2.07281 CenterY=-91.7794 CenterZ=0 NormalX=0 NormalY=0 NormalZ=1 AngleXU=0 Radius=1
    g323: Circle CenterX=-1.92719 CenterY=-91.7794 CenterZ=0 NormalX=0 NormalY=0 NormalZ=1 AngleXU=0 Radius=1
    g324: Circle CenterX=1.57905 CenterY=-89.8542 CenterZ=0 NormalX=0 NormalY=0 NormalZ=1 AngleXU=0 Radius=1
    g325: BSplineCurve PolesCount=3 KnotsCount=2 Degree=2 IsPeriodic=0
    g326: GeomPoint X=2.07281 Y=-91.7794 Z=0
    g327: GeomPoint X=1.57905 Y=-89.8542 Z=0
    g328: LineSegment StartX=2.07281 StartY=-91.7794 StartZ=0 EndX=42.0728 EndY=-91.7794 EndZ=0
    g329: LineSegment StartX=46.0728 StartY=-87.7794 StartZ=0 EndX=46.0728 EndY=-69.424 EndZ=0
    g330: LineSegment StartX=42.5666 StartY=-67.3492 StartZ=0 EndX=1.57905 EndY=-89.8542 EndZ=0
    g331: Circle CenterX=322.073 CenterY=76.4095 CenterZ=0 NormalX=0 NormalY=0 NormalZ=1 AngleXU=0 Radius=4
    g332: BSplineCurve PolesCount=3 KnotsCount=2 Degree=2 IsPeriodic=0
    g333: GeomPoint X=318.073 Y=72.4095 Z=0
    g334: GeomPoint X=322.073 Y=76.4095 Z=0
    g335: Circle CenterX=375.073 CenterY=72.4095 CenterZ=0 NormalX=0 NormalY=0 NormalZ=1 AngleXU=0 Radius=1
    g336: Circle CenterX=375.073 CenterY=76.4095 CenterZ=0 NormalX=0 NormalY=0 NormalZ=1 AngleXU=0 Radius=1
    g337: Circle CenterX=371.073 CenterY=76.4095 CenterZ=0 NormalX=0 NormalY=0 NormalZ=1 AngleXU=0 Radius=1
    g338: BSplineCurve PolesCount=3 KnotsCount=2 Degree=2 IsPeriodic=0
    g339: GeomPoint X=375.073 Y=72.4095 Z=0
    g340: GeomPoint X=371.073 Y=76.4095 Z=0
    g341: LineSegment StartX=322.073 StartY=76.4095 StartZ=0 EndX=371.073 EndY=76.4095 EndZ=0
    g342: LineSegment StartX=318.073 StartY=72.4095 StartZ=0 EndX=318.073 EndY=-47.4805 EndZ=0
    g343: LineSegment StartX=375.073 StartY=72.4095 StartZ=0 EndX=375.073 EndY=-78.7896 EndZ=0
    g344: ArcOfCircle CenterX=-26.9272 CenterY=22.1087 CenterZ=0 NormalX=0 NormalY=0 NormalZ=1 AngleXU=0 Radius=4 StartAngle=5e-16 EndAngle=3.14159
    g345: LineSegment StartX=-22.9272 StartY=22.1087 StartZ=0 EndX=-18.9272 EndY=-83.7794 EndZ=0
    g346: LineSegment StartX=-34.9272 StartY=-83.7794 StartZ=0 EndX=-30.9272 EndY=22.1087 EndZ=0
    g347: LineSegment StartX=383.073 StartY=22.1087 StartZ=0 EndX=387.073 EndY=22.1087 EndZ=0
    g348: LineSegment StartX=399.073 StartY=22.1087 StartZ=0 EndX=395.073 EndY=22.1087 EndZ=0
    g349: LineSegment StartX=395.073 StartY=22.1087 StartZ=0 EndX=399.073 EndY=-83.7794 EndZ=0
    g350: LineSegment StartX=383.073 StartY=-83.7794 StartZ=0 EndX=387.073 EndY=22.1087 EndZ=0
  constraints (577):
    c: Coincident(g0,g2)
    c: Block(g0)
    c: Block(g1)
    c: Vertical(g3)
    c: Vertical(g4)
    c: Block(g4)
    c: Block(g3)
    c: Equal(g6,g7)
    c: Weight(g8) = 1
    c: Equal(g8,g9)
    c: Equal(g8,g10)
    c: InternalAlignment(g8,g11)
    c: InternalAlignment(g9,g11)
    c: InternalAlignment(g10,g11)
    c: InternalAlignment(g12,g11)
    c: InternalAlignment(g13,g11)
    c: Weight(g14) = 1
    c: Equal(g14,g15)
    c: Equal(g14,g16)
    c: InternalAlignment(g14,g17)
    c: InternalAlignment(g15,g17)
    c: InternalAlignment(g16,g17)
    c: InternalAlignment(g18,g17)
    c: InternalAlignment(g19,g17)
    c: Block(g17)
    c: Block(g11)
    c: Weight(g20) = 1
    c: Equal(g20,g21)
    c: Equal(g20,g22)
    c: InternalAlignment(g20,g23)
    c: InternalAlignment(g21,g23)
    c: InternalAlignment(g22,g23)
    c: InternalAlignment(g24,g23)
    c: InternalAlignment(g25,g23)
    c: Weight(g26) = 1
    c: Equal(g26,g27)
    c: Equal(g26,g28)
    c: InternalAlignment(g26,g29)
    c: InternalAlignment(g27,g29)
    c: InternalAlignment(g28,g29)
    c: InternalAlignment(g30,g29)
    c: InternalAlignment(g31,g29)
    c: Block(g29)
    c: Block(g23)
    c: Weight(g32) = 1
    c: Equal(g32,g33)
    c: Equal(g32,g34)
    c: InternalAlignment(g32,g35)
    c: InternalAlignment(g33,g35)
    c: InternalAlignment(g34,g35)
    c: InternalAlignment(g36,g35)
    c: InternalAlignment(g37,g35)
    c: Weight(g38) = 1
    c: Equal(g38,g39)
    c: Equal(g38,g40)
    c: InternalAlignment(g38,g41)
    c: InternalAlignment(g39,g41)
    c: InternalAlignment(g40,g41)
    c: InternalAlignment(g42,g41)
    c: InternalAlignment(g43,g41)
    c: Block(g35)
    c: Block(g41)
    c: Coincident(g44,g4)
    c: Coincident(g44,g3)
    c: Horizontal(g44)
    c: Distance(g44) = 450
    c: Coincident(g45,g4)
    c: Coincident(g45,g3)
    c: Horizontal(g45)
    c: Horizontal(g46)
    c: Coincident(g2,g46)
    c: Block(g46)
    c: Coincident(g1,g46)
    c: Weight(g47) = 1
    c: Equal(g47,g48)
    c: Equal(g47,g49)
    c: InternalAlignment(g47,g50)
    c: InternalAlignment(g48,g50)
    c: InternalAlignment(g49,g50)
    c: InternalAlignment(g51,g50)
    c: InternalAlignment(g52,g50)
    c: Block(g50)
    c: Weight(g53) = 1
    c: Equal(g53,g54)
    c: Equal(g53,g55)
    c: InternalAlignment(g53,g56)
    c: InternalAlignment(g54,g56)
    c: InternalAlignment(g55,g56)
    c: InternalAlignment(g57,g56)
    c: InternalAlignment(g58,g56)
    c: Block(g56)
    c: Weight(g59) = 1
    c: Equal(g59,g60)
    c: Equal(g59,g61)
    c: InternalAlignment(g59,g62)
    c: InternalAlignment(g60,g62)
    c: InternalAlignment(g61,g62)
    c: InternalAlignment(g63,g62)
    c: InternalAlignment(g64,g62)
    c: Block(g62)
    c: Weight(g65) = 1
    c: Equal(g65,g66)
    c: Equal(g65,g67)
    c: InternalAlignment(g65,g68)
    c: InternalAlignment(g66,g68)
    c: InternalAlignment(g67,g68)
    c: InternalAlignment(g69,g68)
    c: InternalAlignment(g70,g68)
    c: Block(g68)
    c: Weight(g71) = 1
    c: Equal(g71,g72)
    c: Equal(g71,g73)
    c: InternalAlignment(g71,g74)
    c: InternalAlignment(g72,g74)
    c: InternalAlignment(g73,g74)
    c: InternalAlignment(g75,g74)
    c: InternalAlignment(g76,g74)
    c: Weight(g77) = 1
    c: Equal(g77,g78)
    c: Equal(g77,g79)
    c: InternalAlignment(g77,g80)
    c: InternalAlignment(g78,g80)
    c: InternalAlignment(g79,g80)
    c: InternalAlignment(g81,g80)
    c: InternalAlignment(g82,g80)
    c: Block(g74)
    c: Block(g80)
    c: Coincident(g83,g74)
    c: Coincident(g83,g80)
    c: Vertical(g83)
    c: Coincident(g84,g74)
    c: Coincident(g84,g56)
    c: Coincident(g85,g56)
    c: Coincident(g85,g80)
    c: Weight(g86) = 1
    c: Equal(g86,g87)
    c: Equal(g86,g88)
    c: InternalAlignment(g86,g89)
    c: InternalAlignment(g87,g89)
    c: InternalAlignment(g88,g89)
    c: InternalAlignment(g90,g89)
    c: InternalAlignment(g91,g89)
    c: Weight(g92) = 1
    c: Equal(g92,g93)
    c: Equal(g92,g94)
    c: InternalAlignment(g92,g95)
    c: InternalAlignment(g93,g95)
    c: InternalAlignment(g94,g95)
    c: InternalAlignment(g96,g95)
    c: InternalAlignment(g97,g95)
    c: Block(g89)
    c: Block(g95)
    c: Coincident(g98,g89)
    c: Coincident(g98,g95)
    c: Vertical(g98)
    c: Coincident(g99,g89)
    c: Coincident(g99,g50)
    c: Coincident(g100,g50)
    c: Coincident(g100,g95)
    c: Weight(g101) = 1
    c: Equal(g101,g102)
    c: Equal(g101,g103)
    c: InternalAlignment(g101,g104)
    c: InternalAlignment(g102,g104)
    c: InternalAlignment(g103,g104)
    c: InternalAlignment(g105,g104)
    c: InternalAlignment(g106,g104)
    c: Weight(g107) = 1
    c: Equal(g107,g108)
    c: Equal(g107,g109)
    c: InternalAlignment(g107,g110)
    c: InternalAlignment(g108,g110)
    c: InternalAlignment(g109,g110)
    c: InternalAlignment(g111,g110)
    c: InternalAlignment(g112,g110)
    c: Block(g104)
    c: Block(g110)
    c: Coincident(g113,g104)
    c: Coincident(g113,g110)
    c: Vertical(g113)
    c: Coincident(g114,g110)
    c: Coincident(g114,g68)
    c: Coincident(g115,g68)
    c: Coincident(g115,g104)
    c: Weight(g116) = 1
    c: Equal(g116,g117)
    c: Equal(g116,g118)
    c: InternalAlignment(g116,g119)
    c: InternalAlignment(g117,g119)
    c: InternalAlignment(g118,g119)
    c: InternalAlignment(g120,g119)
    c: InternalAlignment(g121,g119)
    c: Weight(g122) = 1
    c: Equal(g122,g123)
    c: Equal(g122,g124)
    c: InternalAlignment(g122,g125)
    c: InternalAlignment(g123,g125)
    c: InternalAlignment(g124,g125)
    c: InternalAlignment(g126,g125)
    c: InternalAlignment(g127,g125)
    c: Block(g119)
    c: Block(g125)
    c: Coincident(g128,g119)
    c: Coincident(g128,g125)
    c: Vertical(g128)
    c: Coincident(g129,g125)
    c: Coincident(g129,g62)
    c: Coincident(g130,g62)
    c: Coincident(g130,g119)
    c: Weight(g131) = 1
    c: Equal(g131,g132)
    c: Equal(g131,g133)
    c: InternalAlignment(g131,g134)
    c: InternalAlignment(g132,g134)
    c: InternalAlignment(g133,g134)
    c: InternalAlignment(g135,g134)
    c: InternalAlignment(g136,g134)
    c: Weight(g137) = 1
    c: Equal(g137,g138)
    c: Equal(g137,g139)
    c: InternalAlignment(g137,g140)
    c: InternalAlignment(g138,g140)
    c: InternalAlignment(g139,g140)
    c: InternalAlignment(g141,g140)
    c: InternalAlignment(g142,g140)
    c: Weight(g143) = 1
    c: Equal(g143,g144)
    c: Equal(g143,g145)
    c: InternalAlignment(g143,g146)
    c: InternalAlignment(g144,g146)
    c: InternalAlignment(g145,g146)
    c: InternalAlignment(g147,g146)
    c: InternalAlignment(g148,g146)
    c: Weight(g149) = 1
    c: Equal(g149,g150)
    c: Equal(g149,g151)
    c: InternalAlignment(g149,g152)
    c: InternalAlignment(g150,g152)
    c: InternalAlignment(g151,g152)
    c: InternalAlignment(g153,g152)
    c: InternalAlignment(g154,g152)
    c: Block(g152)
    c: Block(g146)
    c: Block(g140)
    c: Block(g134)
    c: Coincident(g155,g29)
    c: Coincident(g155,g152)
    c: Coincident(g156,g152)
    c: Coincident(g156,g146)
    c: Horizontal(g156)
    c: Coincident(g157,g146)
    c: Coincident(g157,g29)
    c: Vertical(g157)
    c: Coincident(g158,g23)
    c: Coincident(g158,g140)
    c: Vertical(g158)
    c: Coincident(g159,g140)
    c: Coincident(g159,g134)
    c: Horizontal(g159)
    c: Coincident(g160,g134)
    c: Coincident(g160,g23)
    c: Weight(g161) = 1
    c: Equal(g161,g162)
    c: Equal(g161,g163)
    c: InternalAlignment(g161,g164)
    c: InternalAlignment(g162,g164)
    c: InternalAlignment(g163,g164)
    c: InternalAlignment(g165,g164)
    c: InternalAlignment(g166,g164)
    c: Weight(g167) = 1
    c: Equal(g167,g168)
    c: Equal(g167,g169)
    c: InternalAlignment(g167,g170)
    c: InternalAlignment(g168,g170)
    c: InternalAlignment(g169,g170)
    c: InternalAlignment(g171,g170)
    c: InternalAlignment(g172,g170)
    c: Weight(g173) = 1
    c: Equal(g173,g174)
    c: Equal(g173,g175)
    c: InternalAlignment(g173,g176)
    c: InternalAlignment(g174,g176)
    c: InternalAlignment(g175,g176)
    c: InternalAlignment(g177,g176)
    c: InternalAlignment(g178,g176)
    c: Weight(g179) = 1
    c: Equal(g179,g180)
    c: Equal(g179,g181)
    c: InternalAlignment(g179,g182)
    c: InternalAlignment(g180,g182)
    c: InternalAlignment(g181,g182)
    c: InternalAlignment(g183,g182)
    c: InternalAlignment(g184,g182)
    c: Block(g182)
    c: Block(g176)
    c: Block(g170)
    c: Block(g164)
    c: Coincident(g185,g182)
    c: Coincident(g185,g176)
    c: Horizontal(g185)
    c: Coincident(g186,g176)
    c: Coincident(g186,g11)
    c: Vertical(g186)
    c: Coincident(g187,g17)
    c: Coincident(g187,g170)
    c: Vertical(g187)
    c: Coincident(g188,g170)
    c: Coincident(g188,g164)
    c: Horizontal(g188)
    c: Coincident(g189,g164)
    c: Coincident(g189,g17)
    c: Coincident(g190,g11)
    c: Weight(g191) = 1
    c: Equal(g191,g192)
    c: Equal(g191,g193)
    c: InternalAlignment(g191,g194)
    c: InternalAlignment(g192,g194)
    c: InternalAlignment(g193,g194)
    c: InternalAlignment(g195,g194)
    c: InternalAlignment(g196,g194)
    c: Weight(g197) = 1
    c: Equal(g197,g198)
    c: Equal(g197,g199)
    c: InternalAlignment(g197,g200)
    c: InternalAlignment(g198,g200)
    c: InternalAlignment(g199,g200)
    c: InternalAlignment(g201,g200)
    c: InternalAlignment(g202,g200)
    c: Block(g200)
    c: Block(g194)
    c: Coincident(g203,g200)
    c: Coincident(g203,g35)
    c: Coincident(g204,g35)
    c: Coincident(g204,g194)
    c: Coincident(g205,g194)
    c: Coincident(g205,g200)
    c: Vertical(g205)
    c: Weight(g206) = 1
    c: Equal(g206,g207)
    c: Equal(g206,g208)
    c: InternalAlignment(g206,g209)
    c: InternalAlignment(g207,g209)
    c: InternalAlignment(g208,g209)
    c: InternalAlignment(g210,g209)
    c: InternalAlignment(g211,g209)
    c: Weight(g212) = 1
    c: Equal(g212,g213)
    c: Equal(g212,g214)
    c: InternalAlignment(g212,g215)
    c: InternalAlignment(g213,g215)
    c: InternalAlignment(g214,g215)
    c: InternalAlignment(g216,g215)
    c: InternalAlignment(g217,g215)
    c: Block(g215)
    c: Block(g209)
    c: Coincident(g218,g209)
    c: Coincident(g218,g41)
    c: Coincident(g219,g41)
    c: Coincident(g219,g215)
    c: Coincident(g220,g215)
    c: Coincident(g220,g209)
    c: Vertical(g220)
    c: Horizontal(g221)
    c: Block(g221)
    c: Vertical(g222)
    c: Block(g222)
    c: Block(g223)
    c: Weight(g224) = 1
    c: Equal(g224,g225)
    c: Equal(g224,g226)
    c: InternalAlignment(g224,g227)
    c: InternalAlignment(g225,g227)
    c: InternalAlignment(g226,g227)
    c: InternalAlignment(g228,g227)
    c: InternalAlignment(g229,g227)
    c: Weight(g230) = 1
    c: Equal(g230,g231)
    c: Equal(g230,g232)
    c: InternalAlignment(g230,g233)
    c: InternalAlignment(g231,g233)
    c: InternalAlignment(g232,g233)
    c: InternalAlignment(g234,g233)
    c: InternalAlignment(g235,g233)
    c: Weight(g236) = 1
    c: Equal(g236,g237)
    c: Equal(g236,g238)
    c: InternalAlignment(g236,g239)
    c: InternalAlignment(g237,g239)
    c: InternalAlignment(g238,g239)
    c: InternalAlignment(g240,g239)
    c: InternalAlignment(g241,g239)
    c: Weight(g242) = 1
    c: Equal(g242,g243)
    c: Equal(g242,g244)
    c: InternalAlignment(g242,g245)
    c: InternalAlignment(g243,g245)
    c: InternalAlignment(g244,g245)
    c: InternalAlignment(g246,g245)
    c: InternalAlignment(g247,g245)
    c: Block(g227)
    c: Block(g233)
    c: Block(g239)
    c: Block(g245)
    c: Coincident(g248,g233)
    c: Coincident(g248,g227)
    c: Horizontal(g248)
    c: Block(g190)
    c: Weight(g249) = 1
    c: Equal(g249,g250)
    c: Equal(g249,g251)
    c: InternalAlignment(g249,g252)
    c: InternalAlignment(g250,g252)
    c: InternalAlignment(g251,g252)
    c: InternalAlignment(g253,g252)
    c: InternalAlignment(g254,g252)
    c: Weight(g255) = 1
    c: Equal(g255,g256)
    c: Equal(g255,g257)
    c: InternalAlignment(g255,g258)
    c: InternalAlignment(g256,g258)
    c: InternalAlignment(g257,g258)
    c: InternalAlignment(g259,g258)
    c: InternalAlignment(g260,g258)
    c: Block(g252)
    c: Block(g258)
    c: Coincident(g261,g252)
    c: Coincident(g261,g258)
    c: Weight(g262) = 1
    c: Equal(g262,g263)
    c: Equal(g262,g264)
    c: InternalAlignment(g262,g265)
    c: InternalAlignment(g263,g265)
    c: InternalAlignment(g264,g265)
    c: InternalAlignment(g266,g265)
    c: InternalAlignment(g267,g265)
    c: Weight(g268) = 1
    c: Equal(g268,g269)
    c: Equal(g268,g270)
    c: InternalAlignment(g268,g271)
    c: InternalAlignment(g269,g271)
    c: InternalAlignment(g270,g271)
    c: InternalAlignment(g272,g271)
    c: InternalAlignment(g273,g271)
    c: Weight(g274) = 1
    c: Equal(g274,g275)
    c: Equal(g274,g276)
    c: InternalAlignment(g274,g277)
    c: InternalAlignment(g275,g277)
    c: InternalAlignment(g276,g277)
    c: InternalAlignment(g278,g277)
    c: InternalAlignment(g279,g277)
    c: Block(g277)
    c: Block(g271)
    c: Block(g265)
    c: Coincident(g280,g271)
    c: Coincident(g280,g265)
    c: Coincident(g281,g265)
    c: Coincident(g281,g277)
    c: Vertical(g281)
    c: Coincident(g282,g277)
    c: Coincident(g282,g271)
    c: Horizontal(g282)
    c: Weight(g283) = 1
    c: Equal(g283,g284)
    c: InternalAlignment(g283,g285)
    c: InternalAlignment(g284,g285)
    c: InternalAlignment(g286,g285)
    c: InternalAlignment(g287,g285)
    c: Weight(g288) = 1
    c: InternalAlignment(g289,g291)
    c: InternalAlignment(g290,g291)
    c: InternalAlignment(g292,g291)
    c: InternalAlignment(g293,g291)
    c: Weight(g294) = 1
    c: Equal(g294,g295)
    c: Equal(g294,g296)
    c: InternalAlignment(g294,g297)
    c: InternalAlignment(g295,g297)
    c: InternalAlignment(g296,g297)
    c: InternalAlignment(g298,g297)
    c: InternalAlignment(g299,g297)
    c: Equal(g300,g301)
    c: Equal(g300,g302)
    c: InternalAlignment(g300,g303)
    c: InternalAlignment(g301,g303)
    c: InternalAlignment(g302,g303)
    c: InternalAlignment(g304,g303)
    c: InternalAlignment(g305,g303)
    c: Block(g291)
    c: Block(g297)
    c: Block(g303)
    c: Block(g285)
    c: Coincident(g306,g285)
    c: Coincident(g306,g291)
    c: Horizontal(g306)
    c: Coincident(g307,g291)
    c: Coincident(g307,g297)
    c: Vertical(g307)
    c: Coincident(g308,g297)
    c: Coincident(g308,g303)
    c: Horizontal(g308)
    c: Coincident(g309,g303)
    c: Coincident(g309,g285)
    c: Weight(g310) = 1
    c: Equal(g310,g311)
    c: Equal(g310,g312)
    c: InternalAlignment(g310,g313)
    c: InternalAlignment(g311,g313)
    c: InternalAlignment(g312,g313)
    c: InternalAlignment(g314,g313)
    c: InternalAlignment(g315,g313)
    c: Weight(g316) = 1
    c: Equal(g316,g317)
    c: Equal(g316,g318)
    c: InternalAlignment(g316,g319)
    c: InternalAlignment(g317,g319)
    c: InternalAlignment(g318,g319)
    c: InternalAlignment(g320,g319)
    c: InternalAlignment(g321,g319)
    c: Weight(g322) = 1
    c: Equal(g322,g323)
    c: Equal(g322,g324)
    c: InternalAlignment(g322,g325)
    c: InternalAlignment(g323,g325)
    c: InternalAlignment(g324,g325)
    c: InternalAlignment(g326,g325)
    c: InternalAlignment(g327,g325)
    c: Block(g325)
    c: Block(g319)
    c: Block(g313)
    c: Coincident(g328,g325)
    c: Coincident(g328,g319)
    c: Horizontal(g328)
    c: Coincident(g329,g319)
    c: Coincident(g329,g313)
    c: Vertical(g329)
    c: Coincident(g330,g313)
    c: Coincident(g330,g325)
    c: InternalAlignment(g331,g332)
    c: InternalAlignment(g333,g332)
    c: InternalAlignment(g334,g332)
    c: Block(g332)
    c: Equal(g335,g336)
    c: Equal(g335,g337)
    c: InternalAlignment(g335,g338)
    c: InternalAlignment(g336,g338)
    c: InternalAlignment(g337,g338)
    c: InternalAlignment(g339,g338)
    c: InternalAlignment(g340,g338)
    c: Block(g338)
    c: Coincident(g341,g332)
    c: Horizontal(g341)
    c: Block(g341)
    c: Coincident(g342,g332)
    c: Coincident(g342,g258)
    c: Vertical(g342)
    c: Coincident(g343,g338)
    c: Coincident(g343,g252)
    c: Vertical(g343)
    c: Block(g344)
    c: Block(g5)
    c: Distance(g342) = 119.89
    c: Coincident(g345,g344)
    c: Coincident(g345,g5)
    c: Coincident(g346,g5)
    c: Coincident(g346,g344)
    c: Coincident(g347,g6)
    c: Horizontal(g347)
    c: Coincident(g348,g6)
    c: Horizontal(g348)
    c: Distance(g347) = 4
    c: Distance(g348) = 4
    c: Coincident(g349,g348)
    c: Coincident(g349,g7)
    c: Block(g7)
    c: Coincident(g350,g7)
    c: Coincident(g350,g347)
